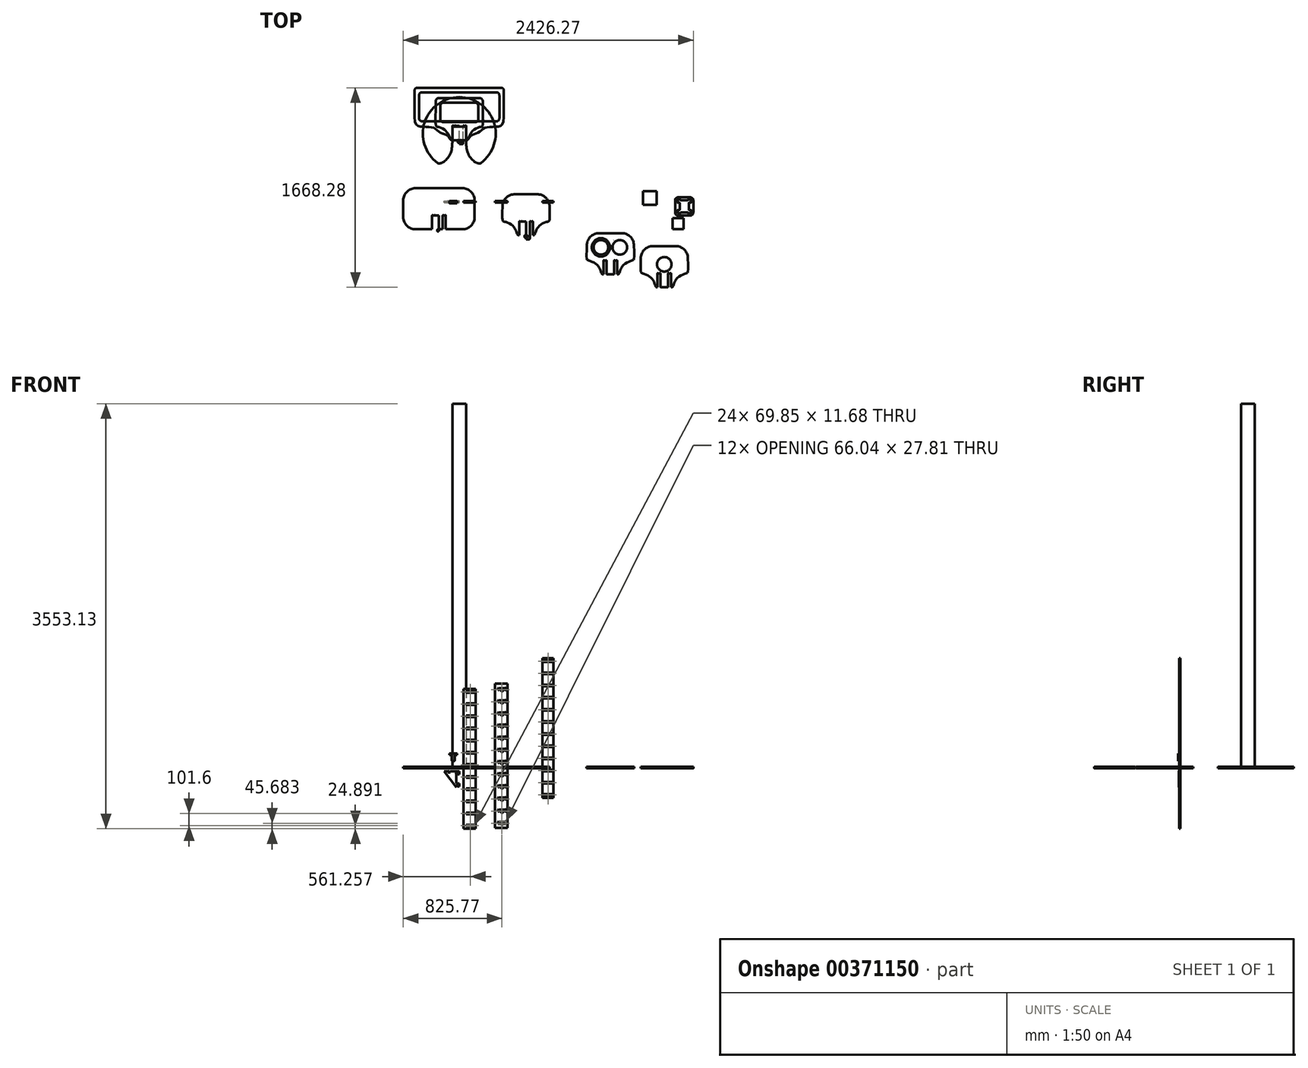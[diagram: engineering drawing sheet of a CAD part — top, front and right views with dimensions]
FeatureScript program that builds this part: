
annotation { "Feature Type Name" : "Feature", "Feature Type Description" : "" }
export const myFeature = defineFeature(function(context is Context, id is Id, definition is map)
    precondition{}
    {
        {
            var Q0;
            Q0=qCreatedBy(makeId("Top.planeOp"),FACE);
            var sketch = newSketch(context, id + "F0", { "sketchPlane" : qUnion([Q0])});
            skLineSegment(sketch, "E0.bottom", {"start": v(-334.1, 107.17) * mm, "end": v(59.6, 107.17) * mm});
            skLineSegment(sketch, "E0.top", {"start": v(-334.1, -235.73) * mm, "end": v(59.6, -235.73) * mm});
            skLineSegment(sketch, "E0.left", {"start": v(-435.7, 5.57) * mm, "end": v(-435.7, -134.13) * mm});
            skLineSegment(sketch, "E0.right", {"start": v(161.2, 5.57) * mm, "end": v(161.2, -134.13) * mm});
            skPoint(sketch, "E1.visualSharp", {"position": v(161.2, 107.17) * mm});
            skArc(sketch, "E1.filletArc", {"start": v(161.2, 5.57) * mm, "mid": v(131.45, 77.42) * mm, "end": v(59.6, 107.17) * mm});
            skPoint(sketch, "E2.visualSharp", {"position": v(-435.7, 107.17) * mm});
            skArc(sketch, "E2.filletArc", {"start": v(-334.1, 107.17) * mm, "mid": v(-405.93, 77.42) * mm, "end": v(-435.7, 5.57) * mm});
            skPoint(sketch, "E3.visualSharp", {"position": v(-435.7, -235.73) * mm});
            skArc(sketch, "E3.filletArc", {"start": v(-435.7, -134.13) * mm, "mid": v(-405.93, -205.97) * mm, "end": v(-334.1, -235.73) * mm});
            skPoint(sketch, "E4.visualSharp", {"position": v(161.2, -235.73) * mm});
            skArc(sketch, "E4.filletArc", {"start": v(59.6, -235.73) * mm, "mid": v(131.45, -205.97) * mm, "end": v(161.2, -134.13) * mm});
            skLineSegment(sketch, "E5", {"start": v(-137.24, -235.73) * mm, "end": v(-137.24, 107.17) * mm, "construction": true});
            skLineSegment(sketch, "E6", {"start": v(-137.24, -235.73) * mm, "end": v(-137.24, -305.02) * mm, "construction": true});
            skLineSegment(sketch, "E7.bottom", {"start": v(-137.24, -270.37) * mm, "end": v(-115.02, -270.37) * mm});
            skLineSegment(sketch, "E7.top", {"start": v(-137.24, -121.43) * mm, "end": v(-105.5, -121.43) * mm});
            skLineSegment(sketch, "E7.left", {"start": v(-137.24, -270.37) * mm, "end": v(-137.24, -121.43) * mm});
            skLineSegment(sketch, "E7.right", {"start": v(-105.5, -260.85) * mm, "end": v(-105.5, -121.43) * mm});
            skLineSegment(sketch, "E8.bottom", {"start": v(-105.5, -121.43) * mm, "end": v(-80.1, -121.43) * mm});
            skLineSegment(sketch, "E8.top", {"start": v(-105.5, -235.73) * mm, "end": v(-80.1, -235.73) * mm});
            skLineSegment(sketch, "E8.left", {"start": v(-105.5, -121.43) * mm, "end": v(-105.5, -235.73) * mm});
            skLineSegment(sketch, "E8.right", {"start": v(-80.1, -121.43) * mm, "end": v(-80.1, -235.73) * mm});
            skLineSegment(sketch, "E9.bottom", {"start": v(-137.24, -235.73) * mm, "end": v(-127.72, -235.73) * mm});
            skLineSegment(sketch, "E9.top", {"start": v(-137.24, -254.5) * mm, "end": v(-127.72, -254.5) * mm});
            skLineSegment(sketch, "E9.left", {"start": v(-137.24, -235.73) * mm, "end": v(-137.24, -254.5) * mm});
            skLineSegment(sketch, "E9.right", {"start": v(-124.54, -238.9) * mm, "end": v(-124.54, -251.32) * mm});
            skArc(sketch, "E10", {"start": v(-99.14, -121.43) * mm, "mid": v(-102.32, -118.25) * mm, "end": v(-105.5, -121.43) * mm});
            skArc(sketch, "E11", {"start": v(-80.1, -121.43) * mm, "mid": v(-83.27, -118.25) * mm, "end": v(-86.44, -121.43) * mm});
            skPoint(sketch, "E12.visualSharp", {"position": v(-124.54, -254.5) * mm});
            skArc(sketch, "E12.filletArc", {"start": v(-127.72, -254.5) * mm, "mid": v(-125.47, -253.57) * mm, "end": v(-124.54, -251.32) * mm});
            skPoint(sketch, "E13.visualSharp", {"position": v(-124.54, -235.73) * mm});
            skArc(sketch, "E13.filletArc", {"start": v(-124.54, -238.9) * mm, "mid": v(-125.47, -236.66) * mm, "end": v(-127.72, -235.73) * mm});
            skPoint(sketch, "E14.visualSharp", {"position": v(-105.5, -270.37) * mm});
            skArc(sketch, "E14.filletArc", {"start": v(-115.02, -270.37) * mm, "mid": v(-108.28, -267.58) * mm, "end": v(-105.5, -260.85) * mm});
            skArc(sketch, "E15.MirrorCS", {"start": v(-149.94, -238.9) * mm, "mid": v(-149.01, -236.66) * mm, "end": v(-146.77, -235.73) * mm});
            skLineSegment(sketch, "E16.MirrorCS", {"start": v(-137.24, -235.73) * mm, "end": v(-146.77, -235.73) * mm});
            skArc(sketch, "E17.MirrorCS", {"start": v(-146.77, -254.5) * mm, "mid": v(-149.01, -253.57) * mm, "end": v(-149.94, -251.32) * mm});
            skArc(sketch, "E18.MirrorCS", {"start": v(-175.34, -121.43) * mm, "mid": v(-172.17, -118.25) * mm, "end": v(-169, -121.43) * mm});
            skLineSegment(sketch, "E19.MirrorCS", {"start": v(-169, -121.43) * mm, "end": v(-194.4, -121.43) * mm});
            skLineSegment(sketch, "E20.MirrorCS", {"start": v(-137.24, -254.5) * mm, "end": v(-146.77, -254.5) * mm});
            skArc(sketch, "E21.MirrorCS", {"start": v(-194.4, -121.43) * mm, "mid": v(-191.22, -118.25) * mm, "end": v(-188.04, -121.43) * mm});
            skArc(sketch, "E22.MirrorCS", {"start": v(-159.47, -270.37) * mm, "mid": v(-166.2, -267.58) * mm, "end": v(-169, -260.85) * mm});
            skLineSegment(sketch, "E23.MirrorCS", {"start": v(-169, -121.43) * mm, "end": v(-169, -235.73) * mm});
            skLineSegment(sketch, "E24.MirrorCS", {"start": v(-169, -235.73) * mm, "end": v(-194.4, -235.73) * mm});
            skLineSegment(sketch, "E25.MirrorCS", {"start": v(-137.24, -270.37) * mm, "end": v(-159.47, -270.37) * mm});
            skLineSegment(sketch, "E26.MirrorCS", {"start": v(-149.94, -238.9) * mm, "end": v(-149.94, -251.32) * mm});
            skPoint(sketch, "E27.MirrorP", {"position": v(-149.94, -235.73) * mm});
            skLineSegment(sketch, "E28.MirrorCS", {"start": v(-137.24, -121.43) * mm, "end": v(-169, -121.43) * mm});
            skPoint(sketch, "E29.MirrorP", {"position": v(-169, -270.37) * mm});
            skLineSegment(sketch, "E30.MirrorCS", {"start": v(-169, -260.85) * mm, "end": v(-169, -121.43) * mm});
            skPoint(sketch, "E31.MirrorP", {"position": v(-149.94, -254.5) * mm});
            skLineSegment(sketch, "E32.MirrorCS", {"start": v(-194.4, -121.43) * mm, "end": v(-194.4, -235.73) * mm});
            skSolve(sketch);
        }
        {
            var Q0;
            {var subQ3=sQuery(id+"F0.wireOp",EDGE,"E15.MirrorCS");Q0=makeQuery(id+"F0.imprint","IMPRINT",FACE,{"disambiguationData":[TD([[makeQuery(id+"F0.imprint","IMPRINT",EDGE,{"derivedFrom":subQ3}),1.0]])]});}
            var Q1;
            {var subQ0=sQuery(id+"F0.wireOp",EDGE,"E7.right");Q1=makeQuery(id+"F0.imprint","IMPRINT",FACE,{"disambiguationData":[TD([[makeQuery(id+"F0.imprint","IMPRINT",EDGE,{"derivedFrom":subQ0}),1.0]])]});}
            var Q2;
            {var subQ2=sQuery(id+"F0.wireOp",EDGE,"E16.MirrorCS");Q2=makeQuery(id+"F0.imprint","IMPRINT",FACE,{"disambiguationData":[TD([[makeQuery(id+"F0.imprint","IMPRINT",EDGE,{"derivedFrom":subQ2}),-1.0]])]});}
            var Q3;
            {var subQ2=sQuery(id+"F0.wireOp",EDGE,"E7.top");Q3=makeQuery(id+"F0.imprint","IMPRINT",FACE,{"disambiguationData":[TD([[makeQuery(id+"F0.imprint","IMPRINT",EDGE,{"derivedFrom":subQ2}),-1.0]])]});}
            var Q4;
            Q4=makeQuery(id+"F0.imprint","IMPRINT",FACE,{"disambiguationData":[TD([[makeQuery(id+"F0.imprint","IMPRINT",EDGE,{"derivedFrom":sQuery(id+"F0.wireOp",EDGE,"E0.bottom")}),-1.0]])]});
            extrude(context, id + "F1", {"entities" : qUnion([Q0, Q1, Q2, Q3, Q4]), "depth" : 11.9 * mm});
        }
        {
            var Q0;
            Q0=qCreatedBy(makeId("Top.planeOp"),FACE);
            var sketch = newSketch(context, id + "F2", { "sketchPlane" : qUnion([Q0])});
            skPoint(sketch, "E33.visualSharp", {"position": v(788.15, 56.35) * mm});
            skArc(sketch, "E33.filletArc", {"start": v(788.15, -45.25) * mm, "mid": v(758.4, 26.59) * mm, "end": v(686.55, 56.35) * mm});
            skPoint(sketch, "E34.visualSharp", {"position": v(788.15, -286.55) * mm});
            skLineSegment(sketch, "E35", {"start": v(591.3, -286.55) * mm, "end": v(591.3, 56.35) * mm, "construction": true});
            skLineSegment(sketch, "E36", {"start": v(591.3, -286.55) * mm, "end": v(591.3, -369.1) * mm, "construction": true});
            skLineSegment(sketch, "E37.top", {"start": v(591.3, -172.25) * mm, "end": v(623.05, -172.25) * mm});
            skLineSegment(sketch, "E37.left", {"start": v(591.3, -327.83) * mm, "end": v(591.3, -172.25) * mm});
            skLineSegment(sketch, "E37.right", {"start": v(623.05, -311.97) * mm, "end": v(623.05, -172.25) * mm});
            skLineSegment(sketch, "E38.bottom", {"start": v(623.05, -172.25) * mm, "end": v(648.45, -172.25) * mm});
            skLineSegment(sketch, "E38.top", {"start": v(623.05, -286.55) * mm, "end": v(648.45, -286.55) * mm});
            skLineSegment(sketch, "E38.left", {"start": v(623.05, -172.25) * mm, "end": v(623.05, -286.55) * mm});
            skLineSegment(sketch, "E38.right", {"start": v(648.45, -172.25) * mm, "end": v(648.45, -286.55) * mm});
            skLineSegment(sketch, "E39.bottom", {"start": v(591.3, -286.55) * mm, "end": v(600.7, -286.55) * mm});
            skLineSegment(sketch, "E39.left", {"start": v(591.3, -286.55) * mm, "end": v(591.3, -311.95) * mm});
            skArc(sketch, "E40", {"start": v(629.4, -172.25) * mm, "mid": v(626.23, -169.08) * mm, "end": v(623.05, -172.25) * mm});
            skPoint(sketch, "E41.visualSharp", {"position": v(604, -311.95) * mm});
            skLineSegment(sketch, "E41.filletArc", {"start": v(604, -311.95) * mm, "end": v(604, -311.95) * mm});
            skPoint(sketch, "E42.visualSharp", {"position": v(604, -286.55) * mm});
            skArc(sketch, "E42.filletArc", {"start": v(604, -289.87) * mm, "mid": v(603.03, -287.52) * mm, "end": v(600.7, -286.55) * mm});
            skPoint(sketch, "E43.visualSharp", {"position": v(623.05, -327.83) * mm});
            skArc(sketch, "E43.filletArc", {"start": v(613.53, -321.48) * mm, "mid": v(620.26, -318.69) * mm, "end": v(623.05, -311.95) * mm});
            skArc(sketch, "E44.MirrorCS", {"start": v(578.6, -289.87) * mm, "mid": v(579.57, -287.52) * mm, "end": v(581.92, -286.55) * mm});
            skLineSegment(sketch, "E45.MirrorCS", {"start": v(591.3, -286.55) * mm, "end": v(581.92, -286.55) * mm});
            skLineSegment(sketch, "E46.MirrorCS", {"start": v(578.6, -311.95) * mm, "end": v(578.6, -311.95) * mm});
            skArc(sketch, "E47.MirrorCS", {"start": v(553.2, -172.25) * mm, "mid": v(556.38, -169.08) * mm, "end": v(559.55, -172.25) * mm});
            skLineSegment(sketch, "E48.MirrorCS", {"start": v(559.55, -172.25) * mm, "end": v(534.15, -172.25) * mm});
            skArc(sketch, "E49.MirrorCS", {"start": v(569.08, -321.48) * mm, "mid": v(562.34, -318.69) * mm, "end": v(559.55, -311.95) * mm});
            skLineSegment(sketch, "E50.MirrorCS", {"start": v(559.55, -172.25) * mm, "end": v(559.55, -286.55) * mm});
            skLineSegment(sketch, "E51.MirrorCS", {"start": v(559.55, -286.55) * mm, "end": v(534.15, -286.55) * mm});
            skPoint(sketch, "E52.MirrorP", {"position": v(578.6, -286.55) * mm});
            skLineSegment(sketch, "E53.MirrorCS", {"start": v(591.3, -172.25) * mm, "end": v(559.55, -172.25) * mm});
            skLineSegment(sketch, "E54.MirrorCS", {"start": v(559.55, -311.95) * mm, "end": v(559.55, -172.25) * mm});
            skLineSegment(sketch, "E55.MirrorCS", {"start": v(534.15, -172.25) * mm, "end": v(534.15, -286.55) * mm});
            skLineSegment(sketch, "E56.MirrorCS", {"start": v(591.3, -321.48) * mm, "end": v(613.53, -321.48) * mm});
            skLineSegment(sketch, "E57.MirrorCS", {"start": v(591.3, -321.48) * mm, "end": v(569.08, -321.48) * mm});
            skFitSpline(sketch, "E58", {"points": [v(648.45, -286.55) * mm, v(655.33, -286.55) * mm, v(665.07, -276.72) * mm, v(673.52, -253) * mm, v(688.14, -225.4) * mm, v(716.4, -196.15) * mm, v(761.89, -175.36) * mm, v(775.2, -171.46) * mm, v(786.25, -163.02) * mm, v(790.22, -124.89) * mm, v(788.15, -45.25) * mm], "startDerivative": vector(133.06, -25.03) * mm, "endDerivative": vector(-44.6, 1613.14) * mm});
            skFitSpline(sketch, "E59.MirrorCS", {"points": [v(534.15, -286.55) * mm, v(527.28, -286.55) * mm, v(517.53, -276.72) * mm, v(509.09, -253) * mm, v(494.47, -225.4) * mm, v(466.2, -196.15) * mm, v(420.72, -175.36) * mm, v(407.4, -171.46) * mm, v(396.36, -163.02) * mm, v(392.39, -124.89) * mm, v(394.45, -45.25) * mm], "startDerivative": vector(-133.06, -25.03) * mm, "endDerivative": vector(44.6, 1613.14) * mm});
            skLineSegment(sketch, "E60.MirrorCS", {"start": v(686.55, 56.35) * mm, "end": v(496.05, 56.35) * mm});
            skPoint(sketch, "E61.MirrorP", {"position": v(394.45, 56.35) * mm});
            skArc(sketch, "E62.MirrorCS", {"start": v(394.45, -45.25) * mm, "mid": v(424.21, 26.59) * mm, "end": v(496.05, 56.35) * mm});
            skPoint(sketch, "E63.MirrorP", {"position": v(394.45, -286.55) * mm});
            skArc(sketch, "E64", {"start": v(648.45, -172.25) * mm, "mid": v(645.28, -169.08) * mm, "end": v(642.1, -172.25) * mm});
            skArc(sketch, "E65", {"start": v(540.5, -172.25) * mm, "mid": v(537.33, -169.08) * mm, "end": v(534.15, -172.25) * mm});
            skLineSegment(sketch, "E66", {"start": v(578.6, -289.87) * mm, "end": v(578.6, -302.15) * mm});
            skLineSegment(sketch, "E67", {"start": v(581.78, -305.32) * mm, "end": v(600.83, -305.32) * mm});
            skLineSegment(sketch, "E68", {"start": v(604, -302.15) * mm, "end": v(604, -289.87) * mm});
            skPoint(sketch, "E69.visualSharp", {"position": v(578.6, -305.32) * mm});
            skArc(sketch, "E69.filletArc", {"start": v(578.6, -302.15) * mm, "mid": v(579.53, -304.4) * mm, "end": v(581.78, -305.32) * mm});
            skPoint(sketch, "E70.visualSharp", {"position": v(604, -305.32) * mm});
            skArc(sketch, "E70.filletArc", {"start": v(600.83, -305.32) * mm, "mid": v(603.07, -304.4) * mm, "end": v(604, -302.15) * mm});
            skLineSegment(sketch, "E71", {"start": v(623.05, -311.97) * mm, "end": v(623.05, -286.55) * mm});
            skPoint(sketch, "E72.orphan", {"position": v(559.55, -318.3) * mm});
            skPoint(sketch, "E73.orphan", {"position": v(623.05, -318.3) * mm});
            skSolve(sketch);
        }
        {
            var Q0;
            {var subQ1=sQuery(id+"F2.wireOp",EDGE,"E37.top");Q0=makeQuery(id+"F2.imprint","IMPRINT",FACE,{"disambiguationData":[TD([[makeQuery(id+"F2.imprint","IMPRINT",EDGE,{"derivedFrom":subQ1}),-1.0]])]});}
            var Q1;
            Q1=makeQuery(id+"F2.imprint","IMPRINT",FACE,{"disambiguationData":[TD([[makeQuery(id+"F2.imprint","IMPRINT",EDGE,{"derivedFrom":sQuery(id+"F2.wireOp",EDGE,"E44.MirrorCS")}),1.0]])]});
            var Q2;
            Q2=makeQuery(id+"F2.imprint","IMPRINT",FACE,{"disambiguationData":[TD([[makeQuery(id+"F2.imprint","IMPRINT",EDGE,{"derivedFrom":sQuery(id+"F2.wireOp",EDGE,"E33.filletArc")}),1.0]])]});
            extrude(context, id + "F3", {"entities" : qUnion([Q0, Q1, Q2]), "depth" : 11.9 * mm});
        }
        {
            var Q0;
            Q0=qCreatedBy(makeId("Top.planeOp"),FACE);
            var sketch = newSketch(context, id + "F4", { "sketchPlane" : qUnion([Q0])});
            skLineSegment(sketch, "E74.bottom", {"start": v(-24.65, 621.06) * mm, "end": v(89.65, 621.06) * mm});
            skLineSegment(sketch, "E74.top", {"start": v(-24.65, 506.76) * mm, "end": v(89.65, 506.76) * mm});
            skLineSegment(sketch, "E74.left", {"start": v(-24.65, 621.06) * mm, "end": v(-24.65, 506.76) * mm});
            skLineSegment(sketch, "E74.right", {"start": v(89.65, 621.06) * mm, "end": v(89.65, 506.76) * mm});
            skSolve(sketch);
        }
        {
            var Q0;
            Q0 = qSketchRegion(id + "F4", true);
            extrude(context, id + "F5", {"entities" : qUnion([Q0]), "depth" : 3048 * mm});
        }
        {
            var Q0;
            Q0=qCreatedBy(makeId("Front.planeOp"),FACE);
            var sketch = newSketch(context, id + "F6", { "sketchPlane" : qUnion([Q0])});
            skLineSegment(sketch, "E75", {"start": v(-93.52, -26.57) * mm, "end": v(8.08, -26.57) * mm});
            skLineSegment(sketch, "E76", {"start": v(8.08, -26.57) * mm, "end": v(8.08, -159.92) * mm});
            skLineSegment(sketch, "E77", {"start": v(8.08, -159.92) * mm, "end": v(-93.52, -26.57) * mm});
            skLineSegment(sketch, "E78", {"start": v(8.08, -26.57) * mm, "end": v(33.48, -26.57) * mm});
            skLineSegment(sketch, "E79", {"start": v(33.48, -26.57) * mm, "end": v(33.48, -51.97) * mm});
            skLineSegment(sketch, "E80", {"start": v(33.48, -51.97) * mm, "end": v(19.64, -51.97) * mm});
            skLineSegment(sketch, "E81", {"start": v(19.64, -51.97) * mm, "end": v(19.64, -39.27) * mm});
            skLineSegment(sketch, "E82", {"start": v(19.64, -39.27) * mm, "end": v(8.08, -39.27) * mm});
            skLineSegment(sketch, "E83", {"start": v(8.08, -128.17) * mm, "end": v(33.48, -128.17) * mm});
            skLineSegment(sketch, "E84", {"start": v(33.48, -128.17) * mm, "end": v(33.48, -153.57) * mm});
            skLineSegment(sketch, "E85", {"start": v(33.48, -153.57) * mm, "end": v(19.64, -153.57) * mm});
            skLineSegment(sketch, "E86", {"start": v(19.64, -153.57) * mm, "end": v(19.64, -140.87) * mm});
            skLineSegment(sketch, "E87", {"start": v(19.64, -140.87) * mm, "end": v(8.08, -140.87) * mm});
            skLineSegment(sketch, "E88", {"start": v(-62.12, -26.57) * mm, "end": v(-49.42, -23.4) * mm});
            skLineSegment(sketch, "E89", {"start": v(-49.42, -23.4) * mm, "end": v(-49.42, -26.57) * mm});
            skLineSegment(sketch, "E90", {"start": v(-49.42, -26.57) * mm, "end": v(-49.42, -26.57) * mm});
            skLineSegment(sketch, "E91", {"start": v(-52.6, -29.75) * mm, "end": v(-59.07, -29.75) * mm});
            skLineSegment(sketch, "E92", {"start": v(-62.25, -32.92) * mm, "end": v(-62.25, -32.92) * mm});
            skLineSegment(sketch, "E93", {"start": v(-59.07, -36.1) * mm, "end": v(-46.25, -36.1) * mm});
            skLineSegment(sketch, "E94", {"start": v(-43.07, -32.92) * mm, "end": v(-43.07, -26.57) * mm});
            skPoint(sketch, "E95.visualSharp", {"position": v(-43.07, -36.1) * mm});
            skArc(sketch, "E95.filletArc", {"start": v(-46.25, -36.1) * mm, "mid": v(-44, -35.17) * mm, "end": v(-43.07, -32.92) * mm});
            skPoint(sketch, "E96.visualSharp", {"position": v(-49.42, -29.75) * mm});
            skArc(sketch, "E96.filletArc", {"start": v(-52.6, -29.75) * mm, "mid": v(-50.35, -28.82) * mm, "end": v(-49.42, -26.57) * mm});
            skPoint(sketch, "E97.visualSharp", {"position": v(-62.25, -29.75) * mm});
            skArc(sketch, "E97.filletArc", {"start": v(-59.07, -29.75) * mm, "mid": v(-61.32, -30.68) * mm, "end": v(-62.25, -32.92) * mm});
            skPoint(sketch, "E98.visualSharp", {"position": v(-62.25, -36.1) * mm});
            skArc(sketch, "E98.filletArc", {"start": v(-62.25, -32.92) * mm, "mid": v(-61.32, -35.17) * mm, "end": v(-59.07, -36.1) * mm});
            skArc(sketch, "E99", {"start": v(8.08, -39.27) * mm, "mid": v(4.9, -42.45) * mm, "end": v(8.08, -45.62) * mm});
            skArc(sketch, "E100", {"start": v(19.64, -45.62) * mm, "mid": v(22.82, -42.45) * mm, "end": v(19.64, -39.27) * mm});
            skArc(sketch, "E101", {"start": v(8.08, -140.87) * mm, "mid": v(4.9, -144.05) * mm, "end": v(8.08, -147.22) * mm});
            skArc(sketch, "E102", {"start": v(19.64, -147.22) * mm, "mid": v(22.82, -144.05) * mm, "end": v(19.64, -140.87) * mm});
            skSolve(sketch);
        }
        {
            var Q0;
            {var subQ0=sQuery(id+"F6.wireOp",EDGE,"E88");Q0=makeQuery(id+"F6.imprint","IMPRINT",FACE,{"disambiguationData":[TD([[makeQuery(id+"F6.imprint","IMPRINT",EDGE,{"derivedFrom":subQ0}),-1.0]])]});}
            var Q1;
            {var subQ1=sQuery(id+"F6.wireOp",EDGE,"E78");Q1=makeQuery(id+"F6.imprint","IMPRINT",FACE,{"disambiguationData":[TD([[makeQuery(id+"F6.imprint","IMPRINT",EDGE,{"derivedFrom":subQ1}),-1.0]])]});}
            var Q2;
            {var subQ1=sQuery(id+"F6.wireOp",EDGE,"E83");Q2=makeQuery(id+"F6.imprint","IMPRINT",FACE,{"disambiguationData":[TD([[makeQuery(id+"F6.imprint","IMPRINT",EDGE,{"derivedFrom":subQ1}),-1.0]])]});}
            var Q3;
            {var subQ0=sQuery(id+"F6.wireOp",EDGE,"E77");Q3=makeQuery(id+"F6.imprint","IMPRINT",FACE,{"disambiguationData":[TD([[makeQuery(id+"F6.imprint","IMPRINT",EDGE,{"derivedFrom":subQ0}),-1.0]])]});}
            extrude(context, id + "F7", {"entities" : qUnion([Q0, Q1, Q2, Q3]), "depth" : 11.9 * mm});
        }
        {
            var Q0;
            Q0=qCreatedBy(makeId("Top.planeOp"),FACE);
            var sketch = newSketch(context, id + "F8", { "sketchPlane" : qUnion([Q0])});
            skLineSegment(sketch, "E103", {"start": v(32.55, 506.79) * mm, "end": v(32.55, 849.69) * mm, "construction": true});
            skLineSegment(sketch, "E104", {"start": v(32.55, 506.79) * mm, "end": v(32.55, 424.24) * mm, "construction": true});
            skLineSegment(sketch, "E105.bottom", {"start": v(32.55, 475.04) * mm, "end": v(54.77, 475.04) * mm});
            skLineSegment(sketch, "E105.top", {"start": v(32.55, 621.09) * mm, "end": v(64.3, 621.09) * mm});
            skLineSegment(sketch, "E105.left", {"start": v(32.55, 465.51) * mm, "end": v(32.55, 621.09) * mm});
            skLineSegment(sketch, "E105.right", {"start": v(64.3, 506.79) * mm, "end": v(64.3, 621.09) * mm});
            skLineSegment(sketch, "E106.bottom", {"start": v(64.3, 621.09) * mm, "end": v(89.7, 621.09) * mm});
            skLineSegment(sketch, "E106.top", {"start": v(64.3, 506.79) * mm, "end": v(89.7, 506.79) * mm});
            skLineSegment(sketch, "E106.left", {"start": v(64.3, 621.09) * mm, "end": v(64.3, 506.79) * mm});
            skLineSegment(sketch, "E106.right", {"start": v(89.7, 621.09) * mm, "end": v(89.7, 506.79) * mm});
            skLineSegment(sketch, "E107.bottom", {"start": v(32.55, 506.79) * mm, "end": v(41.94, 506.79) * mm});
            skLineSegment(sketch, "E107.left", {"start": v(32.55, 506.79) * mm, "end": v(32.55, 481.39) * mm});
            skArc(sketch, "E108", {"start": v(70.65, 621.09) * mm, "mid": v(67.47, 624.26) * mm, "end": v(64.3, 621.09) * mm});
            skPoint(sketch, "E109.visualSharp", {"position": v(45.25, 481.39) * mm});
            skPoint(sketch, "E110.visualSharp", {"position": v(45.25, 506.79) * mm});
            skArc(sketch, "E110.filletArc", {"start": v(45.25, 503.47) * mm, "mid": v(44.28, 505.82) * mm, "end": v(41.94, 506.79) * mm});
            skPoint(sketch, "E111.visualSharp", {"position": v(64.3, 465.51) * mm});
            skArc(sketch, "E111.filletArc", {"start": v(54.77, 475.04) * mm, "mid": v(61.5, 477.83) * mm, "end": v(64.3, 484.56) * mm});
            skLineSegment(sketch, "E112.MirrorCS", {"start": v(78.45, 423.4) * mm, "end": v(78.45, 423.4) * mm});
            skArc(sketch, "E113", {"start": v(89.7, 621.09) * mm, "mid": v(86.52, 624.26) * mm, "end": v(83.35, 621.09) * mm});
            skLineSegment(sketch, "E114", {"start": v(45.25, 491.18) * mm, "end": v(45.25, 503.47) * mm});
            skPoint(sketch, "E115.visualSharp", {"position": v(45.25, 478.07) * mm});
            skArc(sketch, "E115.filletArc", {"start": v(42.07, 488) * mm, "mid": v(44.32, 488.94) * mm, "end": v(45.25, 491.18) * mm});
            skLineSegment(sketch, "E116", {"start": v(64.3, 484.56) * mm, "end": v(64.3, 506.79) * mm});
            skCircle(sketch, "E117", {"center": v(32.55, 563.94) * mm, "radius": 304.8 * mm});
            skPoint(sketch, "E117.centerSnap0", {"position": v(64.3, 563.94) * mm});
            skFitSpline(sketch, "E118", {"points": [v(89.7, 506.79) * mm, v(109.77, 389.43) * mm, v(176.95, 319.57) * mm, v(213.65, 318.78) * mm], "startDerivative": vector(9.59, -299.6) * mm, "endDerivative": vector(116.84, 83.15) * mm});
            skLineSegment(sketch, "E119.MirrorCS", {"start": v(32.55, 506.79) * mm, "end": v(23.16, 506.79) * mm});
            skArc(sketch, "E120.MirrorCS", {"start": v(19.85, 503.47) * mm, "mid": v(20.82, 505.82) * mm, "end": v(23.16, 506.79) * mm});
            skArc(sketch, "E121.MirrorCS", {"start": v(23.02, 488) * mm, "mid": v(20.78, 488.94) * mm, "end": v(19.85, 491.18) * mm});
            skArc(sketch, "E122.MirrorCS", {"start": v(-24.6, 621.09) * mm, "mid": v(-21.43, 624.26) * mm, "end": v(-18.25, 621.09) * mm});
            skArc(sketch, "E123.MirrorCS", {"start": v(-5.55, 621.09) * mm, "mid": v(-2.38, 624.26) * mm, "end": v(0.8, 621.09) * mm});
            skArc(sketch, "E124.MirrorCS", {"start": v(10.32, 475.04) * mm, "mid": v(3.59, 477.83) * mm, "end": v(0.8, 484.56) * mm});
            skLineSegment(sketch, "E125.MirrorCS", {"start": v(0.8, 621.09) * mm, "end": v(-24.6, 621.09) * mm});
            skPoint(sketch, "E126.MirrorP", {"position": v(0.8, 465.51) * mm});
            skPoint(sketch, "E127.MirrorP", {"position": v(19.85, 506.79) * mm});
            skLineSegment(sketch, "E128.MirrorCS", {"start": v(0.8, 484.56) * mm, "end": v(0.8, 506.79) * mm});
            skPoint(sketch, "E129.MirrorP", {"position": v(19.85, 481.39) * mm});
            skLineSegment(sketch, "E130.MirrorCS", {"start": v(0.8, 484.56) * mm, "end": v(0.8, 621.09) * mm});
            skLineSegment(sketch, "E131.MirrorCS", {"start": v(32.55, 475.04) * mm, "end": v(10.32, 475.04) * mm});
            skLineSegment(sketch, "E132.MirrorCS", {"start": v(32.55, 621.09) * mm, "end": v(0.8, 621.09) * mm});
            skPoint(sketch, "E133.MirrorP", {"position": v(19.85, 478.07) * mm});
            skPoint(sketch, "E134.MirrorP", {"position": v(0.8, 563.94) * mm});
            skLineSegment(sketch, "E135.MirrorCS", {"start": v(0.8, 506.79) * mm, "end": v(-24.6, 506.79) * mm});
            skLineSegment(sketch, "E136.MirrorCS", {"start": v(0.8, 621.09) * mm, "end": v(0.8, 506.79) * mm});
            skFitSpline(sketch, "E137.MirrorCS", {"points": [v(-24.6, 506.79) * mm, v(-44.68, 389.43) * mm, v(-111.86, 319.57) * mm, v(-148.56, 318.78) * mm], "startDerivative": vector(-9.59, -299.6) * mm, "endDerivative": vector(-116.84, 83.15) * mm});
            skLineSegment(sketch, "E138.MirrorCS", {"start": v(19.85, 491.18) * mm, "end": v(19.85, 503.47) * mm});
            skLineSegment(sketch, "E139.MirrorCS", {"start": v(-24.6, 621.09) * mm, "end": v(-24.6, 506.79) * mm});
            skLineSegment(sketch, "E140", {"start": v(23.02, 488) * mm, "end": v(42.07, 488) * mm});
            skPoint(sketch, "E141.orphan", {"position": v(0.8, 475.04) * mm});
            skPoint(sketch, "E142.orphan", {"position": v(64.3, 475.04) * mm});
            skSolve(sketch);
        }
        {
            var Q0;
            Q0=makeQuery(id+"F8.imprint","IMPRINT",FACE,{"disambiguationData":[TD([[makeQuery(id+"F8.imprint","IMPRINT",EDGE,{"derivedFrom":sQuery(id+"F8.wireOp",EDGE,"E105.top")}),1.0]])]});
            var Q1;
            {var subQ5=sQuery(id+"F8.wireOp",EDGE,"E105.top");Q1=makeQuery(id+"F8.imprint","IMPRINT",FACE,{"disambiguationData":[TD([[makeQuery(id+"F8.imprint","IMPRINT",EDGE,{"derivedFrom":subQ5}),-1.0]])]});}
            var Q2;
            Q2=makeQuery(id+"F8.imprint","IMPRINT",FACE,{"disambiguationData":[TD([[makeQuery(id+"F8.imprint","IMPRINT",EDGE,{"derivedFrom":sQuery(id+"F8.wireOp",EDGE,"E120.MirrorCS")}),1.0]])]});
            extrude(context, id + "F9", {"entities" : qUnion([Q0, Q1, Q2]), "depth" : 11.9 * mm});
        }
        {
            var Q0;
            Q0=qCreatedBy(makeId("Top.planeOp"),FACE);
            var sketch = newSketch(context, id + "F10", { "sketchPlane" : qUnion([Q0])});
            skPoint(sketch, "E143.visualSharp", {"position": v(229.42, 860.4) * mm});
            skPoint(sketch, "E144.visualSharp", {"position": v(229.42, 506.9) * mm});
            skLineSegment(sketch, "E145", {"start": v(32.57, 506.9) * mm, "end": v(32.57, 860.4) * mm, "construction": true});
            skLineSegment(sketch, "E146", {"start": v(32.57, 506.9) * mm, "end": v(32.57, 475.16) * mm, "construction": true});
            skLineSegment(sketch, "E147.top", {"start": v(32.57, 621.2) * mm, "end": v(64.32, 621.2) * mm});
            skLineSegment(sketch, "E147.left", {"start": v(32.57, 465.63) * mm, "end": v(32.57, 621.2) * mm});
            skLineSegment(sketch, "E147.right", {"start": v(64.32, 484.68) * mm, "end": v(64.32, 621.2) * mm});
            skLineSegment(sketch, "E148.bottom", {"start": v(64.32, 621.2) * mm, "end": v(89.72, 621.2) * mm});
            skLineSegment(sketch, "E148.top", {"start": v(64.32, 506.9) * mm, "end": v(89.72, 506.9) * mm});
            skLineSegment(sketch, "E148.left", {"start": v(64.32, 621.2) * mm, "end": v(64.32, 506.9) * mm});
            skLineSegment(sketch, "E148.right", {"start": v(89.72, 621.2) * mm, "end": v(89.72, 506.9) * mm});
            skLineSegment(sketch, "E149.bottom", {"start": v(32.57, 506.9) * mm, "end": v(41.95, 506.9) * mm});
            skLineSegment(sketch, "E149.left", {"start": v(32.57, 506.9) * mm, "end": v(32.57, 481.5) * mm});
            skArc(sketch, "E150", {"start": v(70.67, 621.2) * mm, "mid": v(67.5, 624.38) * mm, "end": v(64.32, 621.2) * mm});
            skPoint(sketch, "E151.visualSharp", {"position": v(45.27, 481.5) * mm});
            skLineSegment(sketch, "E151.filletArc", {"start": v(17.07, -63.32) * mm, "end": v(17.07, -63.32) * mm});
            skPoint(sketch, "E152.visualSharp", {"position": v(45.27, 506.9) * mm});
            skArc(sketch, "E152.filletArc", {"start": v(45.27, 503.6) * mm, "mid": v(44.3, 505.94) * mm, "end": v(41.95, 506.9) * mm});
            skPoint(sketch, "E153.visualSharp", {"position": v(64.32, 465.63) * mm});
            skArc(sketch, "E153.filletArc", {"start": v(54.8, 475.16) * mm, "mid": v(61.53, 477.95) * mm, "end": v(64.32, 484.68) * mm});
            skArc(sketch, "E154.MirrorCS", {"start": v(19.87, 503.6) * mm, "mid": v(20.84, 505.94) * mm, "end": v(23.18, 506.9) * mm});
            skLineSegment(sketch, "E155.MirrorCS", {"start": v(32.57, 506.9) * mm, "end": v(23.18, 506.9) * mm});
            skLineSegment(sketch, "E156.MirrorCS", {"start": v(-8.33, -63.32) * mm, "end": v(-8.33, -63.32) * mm});
            skArc(sketch, "E157.MirrorCS", {"start": v(-5.53, 621.2) * mm, "mid": v(-2.36, 624.38) * mm, "end": v(0.82, 621.2) * mm});
            skLineSegment(sketch, "E158.MirrorCS", {"start": v(0.82, 621.2) * mm, "end": v(-24.58, 621.2) * mm});
            skLineSegment(sketch, "E159.MirrorCS", {"start": v(0.82, 621.2) * mm, "end": v(0.82, 506.9) * mm});
            skLineSegment(sketch, "E160.MirrorCS", {"start": v(0.82, 506.9) * mm, "end": v(-24.58, 506.9) * mm});
            skLineSegment(sketch, "E161.MirrorCS", {"start": v(32.57, 475.16) * mm, "end": v(10.34, 475.16) * mm});
            skPoint(sketch, "E162.MirrorP", {"position": v(19.87, 506.9) * mm});
            skLineSegment(sketch, "E163.MirrorCS", {"start": v(32.57, 621.2) * mm, "end": v(0.82, 621.2) * mm});
            skPoint(sketch, "E164.MirrorP", {"position": v(0.82, 465.63) * mm});
            skLineSegment(sketch, "E165.MirrorCS", {"start": v(0.82, 484.68) * mm, "end": v(0.82, 621.2) * mm});
            skPoint(sketch, "E166.MirrorP", {"position": v(19.87, 481.5) * mm});
            skLineSegment(sketch, "E167.MirrorCS", {"start": v(-24.58, 621.2) * mm, "end": v(-24.58, 506.9) * mm});
            skArc(sketch, "E168.MirrorCS", {"start": v(10.34, 475.16) * mm, "mid": v(3.6, 477.95) * mm, "end": v(0.82, 484.68) * mm});
            skLineSegment(sketch, "E169.MirrorCS", {"start": v(32.57, 475.16) * mm, "end": v(54.8, 475.16) * mm});
            skFitSpline(sketch, "E170", {"points": [v(89.72, 506.9) * mm, v(96.6, 506.9) * mm, v(106.34, 516.74) * mm, v(114.78, 540.46) * mm, v(129.4, 568.07) * mm, v(157.67, 597.3) * mm, v(203.15, 618.1) * mm, v(216.47, 622) * mm, v(227.51, 630.45) * mm, v(231.48, 668.58) * mm, v(229.42, 758.8) * mm], "startDerivative": vector(133.06, -25.03) * mm, "endDerivative": vector(-44.6, 1613.14) * mm});
            skLineSegment(sketch, "E171.MirrorCS", {"start": v(127.82, 860.4) * mm, "end": v(-62.68, 860.4) * mm});
            skPoint(sketch, "E172.MirrorP", {"position": v(-164.28, 860.4) * mm});
            skPoint(sketch, "E173.MirrorP", {"position": v(-164.28, 506.9) * mm});
            skArc(sketch, "E174", {"start": v(89.72, 621.2) * mm, "mid": v(86.54, 624.38) * mm, "end": v(83.37, 621.2) * mm});
            skArc(sketch, "E175", {"start": v(-18.23, 621.2) * mm, "mid": v(-21.4, 624.38) * mm, "end": v(-24.58, 621.2) * mm});
            skLineSegment(sketch, "E176", {"start": v(19.87, 503.6) * mm, "end": v(19.87, 491.3) * mm});
            skLineSegment(sketch, "E177", {"start": v(23.04, 488.13) * mm, "end": v(42.1, 488.13) * mm});
            skLineSegment(sketch, "E178", {"start": v(45.27, 491.3) * mm, "end": v(45.27, 503.6) * mm});
            skPoint(sketch, "E179.visualSharp", {"position": v(19.87, 488.13) * mm});
            skArc(sketch, "E179.filletArc", {"start": v(19.87, 491.3) * mm, "mid": v(20.8, 489.06) * mm, "end": v(23.04, 488.13) * mm});
            skPoint(sketch, "E180.visualSharp", {"position": v(45.27, 488.13) * mm});
            skArc(sketch, "E180.filletArc", {"start": v(42.1, 488.13) * mm, "mid": v(44.34, 489.06) * mm, "end": v(45.27, 491.3) * mm});
            skLineSegment(sketch, "E181", {"start": v(64.32, 484.68) * mm, "end": v(64.32, 506.9) * mm});
            skLineSegment(sketch, "E182", {"start": v(229.42, 758.8) * mm, "end": v(229.42, 835) * mm});
            skLineSegment(sketch, "E183", {"start": v(127.82, 860.4) * mm, "end": v(204.02, 860.4) * mm});
            skArc(sketch, "E184.filletArc", {"start": v(229.42, 835) * mm, "mid": v(221.98, 852.95) * mm, "end": v(204.02, 860.4) * mm});
            skLineSegment(sketch, "E185.bottom", {"start": v(32.57, 822.3) * mm, "end": v(165.92, 822.3) * mm});
            skLineSegment(sketch, "E185.top", {"start": v(32.57, 659.3) * mm, "end": v(165.92, 659.3) * mm});
            skLineSegment(sketch, "E185.left", {"start": v(32.57, 822.3) * mm, "end": v(32.57, 659.3) * mm});
            skLineSegment(sketch, "E185.right", {"start": v(191.32, 796.9) * mm, "end": v(191.32, 684.7) * mm});
            skPoint(sketch, "E186.visualSharp", {"position": v(191.32, 659.3) * mm});
            skArc(sketch, "E186.filletArc", {"start": v(165.92, 659.3) * mm, "mid": v(183.88, 666.75) * mm, "end": v(191.32, 684.7) * mm});
            skPoint(sketch, "E187.visualSharp", {"position": v(191.32, 822.3) * mm});
            skArc(sketch, "E187.filletArc", {"start": v(191.32, 796.9) * mm, "mid": v(183.88, 814.85) * mm, "end": v(165.92, 822.3) * mm});
            skLineSegment(sketch, "E188.MirrorCS", {"start": v(-164.28, 758.8) * mm, "end": v(-164.28, 835) * mm});
            skArc(sketch, "E189.MirrorCS", {"start": v(-126.18, 796.9) * mm, "mid": v(-118.74, 814.85) * mm, "end": v(-100.78, 822.3) * mm});
            skPoint(sketch, "E190.MirrorP", {"position": v(-126.18, 659.3) * mm});
            skArc(sketch, "E191.MirrorCS", {"start": v(-100.78, 659.3) * mm, "mid": v(-118.74, 666.75) * mm, "end": v(-126.18, 684.7) * mm});
            skPoint(sketch, "E192.MirrorP", {"position": v(-126.18, 822.3) * mm});
            skLineSegment(sketch, "E193.MirrorCS", {"start": v(-62.68, 860.4) * mm, "end": v(127.82, 860.4) * mm});
            skLineSegment(sketch, "E194.MirrorCS", {"start": v(-126.18, 796.9) * mm, "end": v(-126.18, 684.7) * mm});
            skFitSpline(sketch, "E195.MirrorCS", {"points": [v(-24.58, 506.9) * mm, v(-31.46, 506.9) * mm, v(-41.2, 516.74) * mm, v(-49.65, 540.46) * mm, v(-64.27, 568.07) * mm, v(-92.53, 597.3) * mm, v(-138.02, 618.1) * mm, v(-151.34, 622) * mm, v(-162.38, 630.45) * mm, v(-166.35, 668.58) * mm, v(-164.28, 758.8) * mm], "startDerivative": vector(-133.06, -25.03) * mm, "endDerivative": vector(44.6, 1613.14) * mm});
            skLineSegment(sketch, "E196.MirrorCS", {"start": v(32.57, 659.3) * mm, "end": v(-100.78, 659.3) * mm});
            skArc(sketch, "E197.MirrorCS", {"start": v(-164.28, 835) * mm, "mid": v(-156.84, 852.95) * mm, "end": v(-138.88, 860.4) * mm});
            skLineSegment(sketch, "E198.MirrorCS", {"start": v(-62.68, 860.4) * mm, "end": v(-138.88, 860.4) * mm});
            skLineSegment(sketch, "E199.MirrorCS", {"start": v(32.57, 822.3) * mm, "end": v(-100.78, 822.3) * mm});
            skPoint(sketch, "E200.MirrorCS.end.orphan", {"position": v(10.34, 465.63) * mm});
            skPoint(sketch, "E147.bottom.end.orphan", {"position": v(54.8, 465.63) * mm});
            skLineSegment(sketch, "E201.trimOffspring", {"start": v(32.57, 465.63) * mm, "end": v(32.57, 424.36) * mm, "construction": true});
            skPoint(sketch, "E202.orphan", {"position": v(0.82, 475.16) * mm});
            skPoint(sketch, "E203.orphan", {"position": v(64.32, 475.16) * mm});
            skSolve(sketch);
        }
        {
            var Q0;
            {var subQ5=sQuery(id+"F10.wireOp",EDGE,"E147.top");Q0=makeQuery(id+"F10.imprint","IMPRINT",FACE,{"disambiguationData":[TD([[makeQuery(id+"F10.imprint","IMPRINT",EDGE,{"derivedFrom":subQ5}),-1.0]])]});}
            var Q1;
            Q1=makeQuery(id+"F10.imprint","IMPRINT",FACE,{"disambiguationData":[TD([[makeQuery(id+"F10.imprint","IMPRINT",EDGE,{"derivedFrom":sQuery(id+"F10.wireOp",EDGE,"E154.MirrorCS")}),1.0]])]});
            var Q2;
            Q2=makeQuery(id+"F10.imprint","IMPRINT",FACE,{"disambiguationData":[TD([[makeQuery(id+"F10.imprint","IMPRINT",EDGE,{"derivedFrom":sQuery(id+"F10.wireOp",EDGE,"E147.top")}),1.0]])]});
            extrude(context, id + "F11", {"entities" : qUnion([Q0, Q1, Q2]), "depth" : 11.9 * mm});
        }
        {
            var Q0;
            Q0=qCreatedBy(makeId("Top.planeOp"),FACE);
            var sketch = newSketch(context, id + "F12", { "sketchPlane" : qUnion([Q0])});
            skPoint(sketch, "E204.visualSharp", {"position": v(406.26, 947.73) * mm});
            skPoint(sketch, "E205.visualSharp", {"position": v(229.45, 506.82) * mm});
            skLineSegment(sketch, "E206", {"start": v(32.6, 506.82) * mm, "end": v(32.6, 860.3) * mm, "construction": true});
            skLineSegment(sketch, "E207", {"start": v(32.6, 506.82) * mm, "end": v(32.6, 438.24) * mm, "construction": true});
            skLineSegment(sketch, "E208.top", {"start": v(32.6, 628.1) * mm, "end": v(64.35, 628.1) * mm});
            skLineSegment(sketch, "E208.left", {"start": v(32.6, 472.53) * mm, "end": v(32.6, 628.1) * mm});
            skLineSegment(sketch, "E208.right", {"start": v(64.35, 513.8) * mm, "end": v(64.35, 628.1) * mm});
            skLineSegment(sketch, "E209.bottom", {"start": v(64.35, 628.1) * mm, "end": v(89.75, 628.1) * mm});
            skLineSegment(sketch, "E209.top", {"start": v(64.35, 513.8) * mm, "end": v(89.75, 513.8) * mm});
            skLineSegment(sketch, "E209.left", {"start": v(64.35, 628.1) * mm, "end": v(64.35, 513.8) * mm});
            skLineSegment(sketch, "E209.right", {"start": v(89.75, 628.1) * mm, "end": v(89.75, 513.8) * mm});
            skLineSegment(sketch, "E210.bottom", {"start": v(32.6, 513.8) * mm, "end": v(41.98, 513.8) * mm});
            skLineSegment(sketch, "E210.left", {"start": v(32.6, 506.82) * mm, "end": v(32.6, 481.42) * mm});
            skArc(sketch, "E211", {"start": v(70.7, 628.1) * mm, "mid": v(67.52, 631.28) * mm, "end": v(64.35, 628.1) * mm});
            skPoint(sketch, "E212.visualSharp", {"position": v(45.3, 488.4) * mm});
            skLineSegment(sketch, "E212.filletArc", {"start": v(-439.49, 106.29) * mm, "end": v(-439.49, 106.29) * mm});
            skPoint(sketch, "E213.visualSharp", {"position": v(45.3, 513.8) * mm});
            skPoint(sketch, "E214.visualSharp", {"position": v(64.35, 472.53) * mm});
            skArc(sketch, "E214.filletArc", {"start": v(54.82, 482.33) * mm, "mid": v(61.56, 485.12) * mm, "end": v(64.35, 491.86) * mm});
            skArc(sketch, "E215.MirrorCS", {"start": v(19.9, 510.5) * mm, "mid": v(20.87, 512.84) * mm, "end": v(23.2, 513.8) * mm});
            skLineSegment(sketch, "E216.MirrorCS", {"start": v(32.6, 513.8) * mm, "end": v(23.2, 513.8) * mm});
            skLineSegment(sketch, "E217.MirrorCS", {"start": v(-464.89, 106.29) * mm, "end": v(-464.89, 106.29) * mm});
            skArc(sketch, "E218.MirrorCS", {"start": v(-5.5, 628.1) * mm, "mid": v(-2.33, 631.28) * mm, "end": v(0.85, 628.1) * mm});
            skLineSegment(sketch, "E219.MirrorCS", {"start": v(0.85, 628.1) * mm, "end": v(-24.55, 628.1) * mm});
            skLineSegment(sketch, "E220.MirrorCS", {"start": v(0.85, 628.1) * mm, "end": v(0.85, 513.8) * mm});
            skLineSegment(sketch, "E221.MirrorCS", {"start": v(0.85, 513.8) * mm, "end": v(-24.55, 513.8) * mm});
            skPoint(sketch, "E222.MirrorP", {"position": v(19.9, 513.8) * mm});
            skLineSegment(sketch, "E223.MirrorCS", {"start": v(32.6, 628.1) * mm, "end": v(0.85, 628.1) * mm});
            skPoint(sketch, "E224.MirrorP", {"position": v(0.85, 472.53) * mm});
            skLineSegment(sketch, "E225.MirrorCS", {"start": v(0.85, 491.86) * mm, "end": v(0.85, 628.1) * mm});
            skPoint(sketch, "E226.MirrorP", {"position": v(19.9, 488.4) * mm});
            skLineSegment(sketch, "E227.MirrorCS", {"start": v(-24.55, 628.1) * mm, "end": v(-24.55, 513.8) * mm});
            skArc(sketch, "E228.MirrorCS", {"start": v(45.3, 510.5) * mm, "mid": v(44.33, 512.84) * mm, "end": v(41.98, 513.8) * mm});
            skArc(sketch, "E229.MirrorCS", {"start": v(10.37, 482.33) * mm, "mid": v(3.64, 485.12) * mm, "end": v(0.85, 491.86) * mm});
            skLineSegment(sketch, "E230.MirrorCS", {"start": v(32.6, 482.33) * mm, "end": v(54.82, 482.33) * mm});
            skLineSegment(sketch, "E231.MirrorCS", {"start": v(32.6, 482.33) * mm, "end": v(10.37, 482.33) * mm});
            skFitSpline(sketch, "E232", {"points": [v(89.75, 513.8) * mm, v(96.62, 513.8) * mm, v(106.37, 516.65) * mm, v(120.9, 535.75) * mm, v(134, 548.85) * mm, v(171.07, 562.86) * mm, v(208.12, 583.65) * mm, v(239.76, 608.96) * mm, v(300.32, 620.26) * mm, v(374.4, 627.38) * mm, v(406.26, 758.7) * mm], "startDerivative": vector(133.06, -25.03) * mm, "endDerivative": vector(-44.6, 1613.14) * mm});
            skLineSegment(sketch, "E233.MirrorCS", {"start": v(127.85, 947.73) * mm, "end": v(-62.65, 947.73) * mm});
            skPoint(sketch, "E234.MirrorP", {"position": v(-341.07, 947.73) * mm});
            skPoint(sketch, "E235.MirrorP", {"position": v(-164.25, 506.82) * mm});
            skArc(sketch, "E236", {"start": v(89.75, 628.1) * mm, "mid": v(86.57, 631.28) * mm, "end": v(83.4, 628.1) * mm});
            skArc(sketch, "E237", {"start": v(-18.2, 628.1) * mm, "mid": v(-21.38, 631.28) * mm, "end": v(-24.55, 628.1) * mm});
            skLineSegment(sketch, "E238", {"start": v(19.9, 510.5) * mm, "end": v(19.9, 498.07) * mm});
            skLineSegment(sketch, "E239", {"start": v(23.07, 494.9) * mm, "end": v(42.12, 494.9) * mm});
            skLineSegment(sketch, "E240", {"start": v(45.3, 498.07) * mm, "end": v(45.3, 510.5) * mm});
            skPoint(sketch, "E241.visualSharp", {"position": v(19.9, 485.1) * mm});
            skArc(sketch, "E241.filletArc", {"start": v(19.9, 498.07) * mm, "mid": v(20.83, 495.83) * mm, "end": v(23.07, 494.9) * mm});
            skPoint(sketch, "E242.visualSharp", {"position": v(45.3, 485.1) * mm});
            skArc(sketch, "E242.filletArc", {"start": v(42.12, 494.9) * mm, "mid": v(44.37, 495.83) * mm, "end": v(45.3, 498.07) * mm});
            skLineSegment(sketch, "E243", {"start": v(64.35, 491.86) * mm, "end": v(64.35, 513.8) * mm});
            skLineSegment(sketch, "E244", {"start": v(406.26, 758.7) * mm, "end": v(406.26, 922.33) * mm});
            skLineSegment(sketch, "E245", {"start": v(127.85, 947.73) * mm, "end": v(380.86, 947.73) * mm});
            skArc(sketch, "E246.filletArc", {"start": v(406.26, 922.33) * mm, "mid": v(398.82, 940.3) * mm, "end": v(380.86, 947.73) * mm});
            skLineSegment(sketch, "E247.bottom", {"start": v(32.6, 909.63) * mm, "end": v(342.76, 909.63) * mm});
            skLineSegment(sketch, "E247.top", {"start": v(32.6, 666.2) * mm, "end": v(342.76, 666.2) * mm});
            skLineSegment(sketch, "E247.left", {"start": v(32.6, 909.63) * mm, "end": v(32.6, 666.2) * mm});
            skLineSegment(sketch, "E247.right", {"start": v(368.16, 884.23) * mm, "end": v(368.16, 691.6) * mm});
            skPoint(sketch, "E248.visualSharp", {"position": v(368.16, 666.2) * mm});
            skArc(sketch, "E248.filletArc", {"start": v(342.76, 666.2) * mm, "mid": v(360.72, 673.64) * mm, "end": v(368.16, 691.6) * mm});
            skPoint(sketch, "E249.visualSharp", {"position": v(368.16, 909.63) * mm});
            skArc(sketch, "E249.filletArc", {"start": v(368.16, 884.23) * mm, "mid": v(360.72, 902.2) * mm, "end": v(342.76, 909.63) * mm});
            skLineSegment(sketch, "E250.MirrorCS", {"start": v(-341.07, 758.7) * mm, "end": v(-341.07, 922.33) * mm});
            skArc(sketch, "E251.MirrorCS", {"start": v(-302.97, 884.23) * mm, "mid": v(-295.53, 902.2) * mm, "end": v(-277.57, 909.63) * mm});
            skPoint(sketch, "E252.MirrorP", {"position": v(-302.97, 666.2) * mm});
            skArc(sketch, "E253.MirrorCS", {"start": v(-277.57, 666.2) * mm, "mid": v(-295.53, 673.64) * mm, "end": v(-302.97, 691.6) * mm});
            skPoint(sketch, "E254.MirrorP", {"position": v(-302.97, 909.63) * mm});
            skLineSegment(sketch, "E255.MirrorCS", {"start": v(-62.65, 947.73) * mm, "end": v(127.85, 947.73) * mm});
            skLineSegment(sketch, "E256.MirrorCS", {"start": v(-302.97, 884.23) * mm, "end": v(-302.97, 691.6) * mm});
            skFitSpline(sketch, "E257.MirrorCS", {"points": [v(-24.55, 513.8) * mm, v(-31.43, 513.8) * mm, v(-41.18, 516.65) * mm, v(-55.71, 535.75) * mm, v(-68.82, 548.85) * mm, v(-105.87, 562.86) * mm, v(-142.93, 583.65) * mm, v(-174.57, 608.96) * mm, v(-235.13, 620.26) * mm, v(-309.2, 627.38) * mm, v(-341.07, 758.7) * mm], "startDerivative": vector(-133.06, -25.03) * mm, "endDerivative": vector(44.6, 1613.14) * mm});
            skLineSegment(sketch, "E258.MirrorCS", {"start": v(32.6, 666.2) * mm, "end": v(-277.57, 666.2) * mm});
            skArc(sketch, "E259.MirrorCS", {"start": v(-341.07, 922.33) * mm, "mid": v(-333.63, 940.3) * mm, "end": v(-315.67, 947.73) * mm});
            skLineSegment(sketch, "E260.MirrorCS", {"start": v(-62.65, 947.73) * mm, "end": v(-315.67, 947.73) * mm});
            skLineSegment(sketch, "E261.MirrorCS", {"start": v(32.6, 909.63) * mm, "end": v(-277.57, 909.63) * mm});
            skLineSegment(sketch, "E262", {"start": v(0.85, 513.8) * mm, "end": v(64.35, 513.8) * mm, "construction": true});
            skPoint(sketch, "E263.orphan", {"position": v(0.85, 482.06) * mm});
            skPoint(sketch, "E264.orphan", {"position": v(64.35, 482.06) * mm});
            skSolve(sketch);
        }
        {
            var Q0;
            {var subQ5=sQuery(id+"F12.wireOp",EDGE,"E208.top");Q0=makeQuery(id+"F12.imprint","IMPRINT",FACE,{"disambiguationData":[TD([[makeQuery(id+"F12.imprint","IMPRINT",EDGE,{"derivedFrom":subQ5}),-1.0]])]});}
            var Q1;
            Q1=makeQuery(id+"F12.imprint","IMPRINT",FACE,{"disambiguationData":[TD([[makeQuery(id+"F12.imprint","IMPRINT",EDGE,{"derivedFrom":sQuery(id+"F12.wireOp",EDGE,"d7ea122c-9ec8-4e4a-8ab8-e34f7a07d9ba.MirrorCS")}),1.0]])]});
            var Q2;
            Q2=makeQuery(id+"F12.imprint","IMPRINT",FACE,{"disambiguationData":[TD([[makeQuery(id+"F12.imprint","IMPRINT",EDGE,{"derivedFrom":sQuery(id+"F12.wireOp",EDGE,"E208.top")}),1.0]])]});
            var Q3;
            Q3=makeQuery(id+"F12.imprint","IMPRINT",FACE,{"disambiguationData":[TD([[makeQuery(id+"F12.imprint","IMPRINT",EDGE,{"derivedFrom":sQuery(id+"F12.wireOp",EDGE,"E215.MirrorCS")}),1.0]])]});
            extrude(context, id + "F13", {"entities" : qUnion([Q0, Q1, Q2, Q3]), "depth" : 11.9 * mm});
        }
        {
            var Q0;
            Q0=qCreatedBy(makeId("Front.planeOp"),FACE);
            var sketch = newSketch(context, id + "F14", { "sketchPlane" : qUnion([Q0])});
            skLineSegment(sketch, "E265.bottom", {"start": v(-29.21, 112.4) * mm, "end": v(-6.35, 112.4) * mm});
            skLineSegment(sketch, "E265.top", {"start": v(-26.04, 61.6) * mm, "end": v(-9.52, 61.6) * mm});
            skLineSegment(sketch, "E265.left", {"start": v(-29.21, 112.4) * mm, "end": v(-29.21, 64.78) * mm});
            skLineSegment(sketch, "E265.right", {"start": v(-6.35, 112.4) * mm, "end": v(-6.35, 64.78) * mm});
            skLineSegment(sketch, "E266.bottom", {"start": v(10.8, 125.1) * mm, "end": v(-46.36, 125.1) * mm});
            skLineSegment(sketch, "E266.top", {"start": v(13.97, 112.4) * mm, "end": v(0, 112.4) * mm});
            skLineSegment(sketch, "E266.left", {"start": v(13.97, 121.93) * mm, "end": v(13.97, 112.4) * mm});
            skLineSegment(sketch, "E266.right", {"start": v(-49.53, 121.93) * mm, "end": v(-49.53, 112.4) * mm});
            skPoint(sketch, "E267", {"position": v(-5.08, 121.93) * mm});
            skArc(sketch, "E268", {"start": v(0, 112.4) * mm, "mid": v(-3.17, 115.58) * mm, "end": v(-6.35, 112.4) * mm});
            skArc(sketch, "E269", {"start": v(-29.2, 112.4) * mm, "mid": v(-32.38, 115.58) * mm, "end": v(-35.56, 112.4) * mm});
            skPoint(sketch, "E270.visualSharp", {"position": v(-49.53, 121.93) * mm});
            skArc(sketch, "E270.filletArc", {"start": v(-46.36, 125.1) * mm, "mid": v(-48.6, 124.17) * mm, "end": v(-49.53, 121.93) * mm});
            skPoint(sketch, "E271.visualSharp", {"position": v(13.97, 125.1) * mm});
            skArc(sketch, "E271.filletArc", {"start": v(13.97, 121.93) * mm, "mid": v(13.04, 124.17) * mm, "end": v(10.8, 125.1) * mm});
            skPoint(sketch, "E272.visualSharp", {"position": v(-6.35, 61.6) * mm});
            skArc(sketch, "E272.filletArc", {"start": v(-9.52, 61.6) * mm, "mid": v(-7.28, 62.53) * mm, "end": v(-6.35, 64.78) * mm});
            skPoint(sketch, "E273.visualSharp", {"position": v(-29.21, 61.6) * mm});
            skArc(sketch, "E273.filletArc", {"start": v(-29.21, 64.78) * mm, "mid": v(-28.28, 62.53) * mm, "end": v(-26.04, 61.6) * mm});
            skLineSegment(sketch, "E274.trimOffspring", {"start": v(-35.56, 112.4) * mm, "end": v(-49.53, 112.4) * mm});
            skLineSegment(sketch, "E275.trimOffspring", {"start": v(-6.35, 112.4) * mm, "end": v(-29.21, 112.4) * mm});
            skSolve(sketch);
        }
        {
            var Q0;
            Q0 = qSketchRegion(id + "F14", true);
            extrude(context, id + "F15", {"entities" : qUnion([Q0]), "depth" : 18.77 * mm});
        }
        {
            var Q0;
            Q0=qCreatedBy(makeId("Front.planeOp"),FACE);
            var sketch = newSketch(context, id + "F16", { "sketchPlane" : qUnion([Q0])});
            skLineSegment(sketch, "E276.bottom", {"start": v(68.42, 663.27) * mm, "end": v(170.78, 663.27) * mm});
            skLineSegment(sketch, "E276.top", {"start": v(68.42, -505.13) * mm, "end": v(170.78, -505.13) * mm});
            skLineSegment(sketch, "E276.left", {"start": v(68.42, 663.27) * mm, "end": v(68.42, -505.13) * mm});
            skLineSegment(sketch, "E276.right", {"start": v(170.78, 663.27) * mm, "end": v(170.78, -505.13) * mm});
            skLineSegment(sketch, "E277.bottom", {"start": v(90.64, -474.4) * mm, "end": v(160.5, -474.4) * mm});
            skLineSegment(sketch, "E277.top", {"start": v(90.64, -486.08) * mm, "end": v(160.5, -486.08) * mm});
            skLineSegment(sketch, "E277.left", {"start": v(90.64, -474.4) * mm, "end": v(90.64, -486.08) * mm});
            skLineSegment(sketch, "E277.right", {"start": v(160.5, -474.4) * mm, "end": v(160.5, -486.08) * mm});
            skLineSegment(sketch, "E278", {"start": v(119.6, -505.13) * mm, "end": v(119.6, -373.16) * mm, "construction": true});
            skLineSegment(sketch, "E279", {"start": v(68.42, -346.92) * mm, "end": v(182.72, -346.92) * mm, "construction": true});
            skLineSegment(sketch, "E280", {"start": v(125.57, -346.92) * mm, "end": v(125.57, -534.23) * mm, "construction": true});
            skLineSegment(sketch, "E281.0.1.0", {"start": v(160.5, -372.8) * mm, "end": v(160.5, -384.48) * mm});
            skLineSegment(sketch, "E281.0.1.1", {"start": v(90.64, -384.48) * mm, "end": v(160.5, -384.48) * mm});
            skLineSegment(sketch, "E281.0.1.2", {"start": v(90.64, -372.8) * mm, "end": v(160.5, -372.8) * mm});
            skLineSegment(sketch, "E281.0.1.3", {"start": v(90.64, -372.8) * mm, "end": v(90.64, -384.48) * mm});
            skLineSegment(sketch, "E281.0.2.0", {"start": v(160.5, -271.2) * mm, "end": v(160.5, -282.88) * mm});
            skLineSegment(sketch, "E281.0.2.1", {"start": v(90.64, -282.88) * mm, "end": v(160.5, -282.88) * mm});
            skLineSegment(sketch, "E281.0.2.2", {"start": v(90.64, -271.2) * mm, "end": v(160.5, -271.2) * mm});
            skLineSegment(sketch, "E281.0.2.3", {"start": v(90.64, -271.2) * mm, "end": v(90.64, -282.88) * mm});
            skLineSegment(sketch, "E281.0.3.0", {"start": v(160.5, -169.6) * mm, "end": v(160.5, -181.28) * mm});
            skLineSegment(sketch, "E281.0.3.1", {"start": v(90.64, -181.28) * mm, "end": v(160.5, -181.28) * mm});
            skLineSegment(sketch, "E281.0.3.2", {"start": v(90.64, -169.6) * mm, "end": v(160.5, -169.6) * mm});
            skLineSegment(sketch, "E281.0.3.3", {"start": v(90.64, -169.6) * mm, "end": v(90.64, -181.28) * mm});
            skLineSegment(sketch, "E281.0.4.0", {"start": v(160.5, -68) * mm, "end": v(160.5, -79.68) * mm});
            skLineSegment(sketch, "E281.0.4.1", {"start": v(90.64, -79.68) * mm, "end": v(160.5, -79.68) * mm});
            skLineSegment(sketch, "E281.0.4.2", {"start": v(90.64, -68) * mm, "end": v(160.5, -68) * mm});
            skLineSegment(sketch, "E281.0.4.3", {"start": v(90.64, -68) * mm, "end": v(90.64, -79.68) * mm});
            skLineSegment(sketch, "E281.0.5.0", {"start": v(160.5, 33.6) * mm, "end": v(160.5, 21.92) * mm});
            skLineSegment(sketch, "E281.0.5.1", {"start": v(90.64, 21.92) * mm, "end": v(160.5, 21.92) * mm});
            skLineSegment(sketch, "E281.0.5.2", {"start": v(90.64, 33.6) * mm, "end": v(160.5, 33.6) * mm});
            skLineSegment(sketch, "E281.0.5.3", {"start": v(90.64, 33.6) * mm, "end": v(90.64, 21.92) * mm});
            skLineSegment(sketch, "E281.0.6.0", {"start": v(160.5, 135.2) * mm, "end": v(160.5, 123.52) * mm});
            skLineSegment(sketch, "E281.0.6.1", {"start": v(90.64, 123.52) * mm, "end": v(160.5, 123.52) * mm});
            skLineSegment(sketch, "E281.0.6.2", {"start": v(90.64, 135.2) * mm, "end": v(160.5, 135.2) * mm});
            skLineSegment(sketch, "E281.0.6.3", {"start": v(90.64, 135.2) * mm, "end": v(90.64, 123.52) * mm});
            skLineSegment(sketch, "E281.0.7.0", {"start": v(160.5, 236.8) * mm, "end": v(160.5, 225.12) * mm});
            skLineSegment(sketch, "E281.0.7.1", {"start": v(90.64, 225.12) * mm, "end": v(160.5, 225.12) * mm});
            skLineSegment(sketch, "E281.0.7.2", {"start": v(90.64, 236.8) * mm, "end": v(160.5, 236.8) * mm});
            skLineSegment(sketch, "E281.0.7.3", {"start": v(90.64, 236.8) * mm, "end": v(90.64, 225.12) * mm});
            skLineSegment(sketch, "E281.0.8.0", {"start": v(160.5, 338.4) * mm, "end": v(160.5, 326.72) * mm});
            skLineSegment(sketch, "E281.0.8.1", {"start": v(90.64, 326.72) * mm, "end": v(160.5, 326.72) * mm});
            skLineSegment(sketch, "E281.0.8.2", {"start": v(90.64, 338.4) * mm, "end": v(160.5, 338.4) * mm});
            skLineSegment(sketch, "E281.0.8.3", {"start": v(90.64, 338.4) * mm, "end": v(90.64, 326.72) * mm});
            skLineSegment(sketch, "E281.0.9.0", {"start": v(160.5, 440) * mm, "end": v(160.5, 428.32) * mm});
            skLineSegment(sketch, "E281.0.9.1", {"start": v(90.64, 428.32) * mm, "end": v(160.5, 428.32) * mm});
            skLineSegment(sketch, "E281.0.9.2", {"start": v(90.64, 440) * mm, "end": v(160.5, 440) * mm});
            skLineSegment(sketch, "E281.0.9.3", {"start": v(90.64, 440) * mm, "end": v(90.64, 428.32) * mm});
            skLineSegment(sketch, "E281.0.10.0", {"start": v(160.5, 541.6) * mm, "end": v(160.5, 529.92) * mm});
            skLineSegment(sketch, "E281.0.10.1", {"start": v(90.64, 529.92) * mm, "end": v(160.5, 529.92) * mm});
            skLineSegment(sketch, "E281.0.10.2", {"start": v(90.64, 541.6) * mm, "end": v(160.5, 541.6) * mm});
            skLineSegment(sketch, "E281.0.10.3", {"start": v(90.64, 541.6) * mm, "end": v(90.64, 529.92) * mm});
            skLineSegment(sketch, "E281.0.11.0", {"start": v(160.5, 643.2) * mm, "end": v(160.5, 631.52) * mm});
            skLineSegment(sketch, "E281.0.11.1", {"start": v(90.64, 631.52) * mm, "end": v(160.5, 631.52) * mm});
            skLineSegment(sketch, "E281.0.11.2", {"start": v(90.64, 643.2) * mm, "end": v(160.5, 643.2) * mm});
            skLineSegment(sketch, "E281.0.11.3", {"start": v(90.64, 643.2) * mm, "end": v(90.64, 631.52) * mm});
            skLineSegment(sketch, "E281.direction1", {"start": v(90.64, -486.08) * mm, "end": v(116.04, -486.08) * mm, "construction": true});
            skLineSegment(sketch, "E281.direction2", {"start": v(90.64, -486.08) * mm, "end": v(90.64, -384.48) * mm, "construction": true});
            skLineSegment(sketch, "E282.bottom", {"start": v(729.87, 922.14) * mm, "end": v(820.9, 922.14) * mm});
            skLineSegment(sketch, "E282.top", {"start": v(729.87, -246.26) * mm, "end": v(820.9, -246.26) * mm});
            skLineSegment(sketch, "E282.left", {"start": v(729.87, 922.14) * mm, "end": v(729.87, -246.26) * mm});
            skLineSegment(sketch, "E282.right", {"start": v(820.9, 922.14) * mm, "end": v(820.9, -246.26) * mm});
            skLineSegment(sketch, "E283.bottom", {"start": v(740.46, -215.53) * mm, "end": v(810.31, -215.53) * mm});
            skLineSegment(sketch, "E283.top", {"start": v(740.46, -227.21) * mm, "end": v(810.31, -227.21) * mm});
            skLineSegment(sketch, "E283.left", {"start": v(740.46, -215.53) * mm, "end": v(740.46, -227.21) * mm});
            skLineSegment(sketch, "E283.right", {"start": v(810.31, -215.53) * mm, "end": v(810.31, -227.21) * mm});
            skLineSegment(sketch, "E284.direction1", {"start": v(740.46, -227.21) * mm, "end": v(777.5, -227.21) * mm, "construction": true});
            skLineSegment(sketch, "E285.0.1.0", {"start": v(740.46, -113.93) * mm, "end": v(810.31, -113.93) * mm});
            skLineSegment(sketch, "E285.0.1.1", {"start": v(810.31, -113.93) * mm, "end": v(810.31, -125.61) * mm});
            skLineSegment(sketch, "E285.0.1.2", {"start": v(740.46, -125.61) * mm, "end": v(810.31, -125.61) * mm});
            skLineSegment(sketch, "E285.0.1.3", {"start": v(740.46, -113.93) * mm, "end": v(740.46, -125.61) * mm});
            skLineSegment(sketch, "E285.0.2.0", {"start": v(740.46, -12.33) * mm, "end": v(810.31, -12.33) * mm});
            skLineSegment(sketch, "E285.0.2.1", {"start": v(810.31, -12.33) * mm, "end": v(810.31, -24.01) * mm});
            skLineSegment(sketch, "E285.0.2.2", {"start": v(740.46, -24.01) * mm, "end": v(810.31, -24.01) * mm});
            skLineSegment(sketch, "E285.0.2.3", {"start": v(740.46, -12.33) * mm, "end": v(740.46, -24.01) * mm});
            skLineSegment(sketch, "E285.0.3.0", {"start": v(740.46, 89.27) * mm, "end": v(810.31, 89.27) * mm});
            skLineSegment(sketch, "E285.0.3.1", {"start": v(810.31, 89.27) * mm, "end": v(810.31, 77.59) * mm});
            skLineSegment(sketch, "E285.0.3.2", {"start": v(740.46, 77.59) * mm, "end": v(810.31, 77.59) * mm});
            skLineSegment(sketch, "E285.0.3.3", {"start": v(740.46, 89.27) * mm, "end": v(740.46, 77.59) * mm});
            skLineSegment(sketch, "E285.0.4.0", {"start": v(740.46, 190.87) * mm, "end": v(810.31, 190.87) * mm});
            skLineSegment(sketch, "E285.0.4.1", {"start": v(810.31, 190.87) * mm, "end": v(810.31, 179.19) * mm});
            skLineSegment(sketch, "E285.0.4.2", {"start": v(740.46, 179.19) * mm, "end": v(810.31, 179.19) * mm});
            skLineSegment(sketch, "E285.0.4.3", {"start": v(740.46, 190.87) * mm, "end": v(740.46, 179.19) * mm});
            skLineSegment(sketch, "E285.0.5.0", {"start": v(740.46, 292.47) * mm, "end": v(810.31, 292.47) * mm});
            skLineSegment(sketch, "E285.0.5.1", {"start": v(810.31, 292.47) * mm, "end": v(810.31, 280.79) * mm});
            skLineSegment(sketch, "E285.0.5.2", {"start": v(740.46, 280.79) * mm, "end": v(810.31, 280.79) * mm});
            skLineSegment(sketch, "E285.0.5.3", {"start": v(740.46, 292.47) * mm, "end": v(740.46, 280.79) * mm});
            skLineSegment(sketch, "E285.0.6.0", {"start": v(740.46, 394.07) * mm, "end": v(810.31, 394.07) * mm});
            skLineSegment(sketch, "E285.0.6.1", {"start": v(810.31, 394.07) * mm, "end": v(810.31, 382.39) * mm});
            skLineSegment(sketch, "E285.0.6.2", {"start": v(740.46, 382.39) * mm, "end": v(810.31, 382.39) * mm});
            skLineSegment(sketch, "E285.0.6.3", {"start": v(740.46, 394.07) * mm, "end": v(740.46, 382.39) * mm});
            skLineSegment(sketch, "E285.0.7.0", {"start": v(740.46, 495.67) * mm, "end": v(810.31, 495.67) * mm});
            skLineSegment(sketch, "E285.0.7.1", {"start": v(810.31, 495.67) * mm, "end": v(810.31, 483.99) * mm});
            skLineSegment(sketch, "E285.0.7.2", {"start": v(740.46, 483.99) * mm, "end": v(810.31, 483.99) * mm});
            skLineSegment(sketch, "E285.0.7.3", {"start": v(740.46, 495.67) * mm, "end": v(740.46, 483.99) * mm});
            skLineSegment(sketch, "E285.0.8.0", {"start": v(740.46, 597.27) * mm, "end": v(810.31, 597.27) * mm});
            skLineSegment(sketch, "E285.0.8.1", {"start": v(810.31, 597.27) * mm, "end": v(810.31, 585.59) * mm});
            skLineSegment(sketch, "E285.0.8.2", {"start": v(740.46, 585.59) * mm, "end": v(810.31, 585.59) * mm});
            skLineSegment(sketch, "E285.0.8.3", {"start": v(740.46, 597.27) * mm, "end": v(740.46, 585.59) * mm});
            skLineSegment(sketch, "E285.0.9.0", {"start": v(740.46, 698.87) * mm, "end": v(810.31, 698.87) * mm});
            skLineSegment(sketch, "E285.0.9.1", {"start": v(810.31, 698.87) * mm, "end": v(810.31, 687.19) * mm});
            skLineSegment(sketch, "E285.0.9.2", {"start": v(740.46, 687.19) * mm, "end": v(810.31, 687.19) * mm});
            skLineSegment(sketch, "E285.0.9.3", {"start": v(740.46, 698.87) * mm, "end": v(740.46, 687.19) * mm});
            skLineSegment(sketch, "E285.0.10.0", {"start": v(740.46, 800.47) * mm, "end": v(810.31, 800.47) * mm});
            skLineSegment(sketch, "E285.0.10.1", {"start": v(810.31, 800.47) * mm, "end": v(810.31, 788.79) * mm});
            skLineSegment(sketch, "E285.0.10.2", {"start": v(740.46, 788.79) * mm, "end": v(810.31, 788.79) * mm});
            skLineSegment(sketch, "E285.0.10.3", {"start": v(740.46, 800.47) * mm, "end": v(740.46, 788.79) * mm});
            skLineSegment(sketch, "E285.0.11.0", {"start": v(740.46, 902.07) * mm, "end": v(810.31, 902.07) * mm});
            skLineSegment(sketch, "E285.0.11.1", {"start": v(810.31, 902.07) * mm, "end": v(810.31, 890.39) * mm});
            skLineSegment(sketch, "E285.0.11.2", {"start": v(740.46, 890.39) * mm, "end": v(810.31, 890.39) * mm});
            skLineSegment(sketch, "E285.0.11.3", {"start": v(740.46, 902.07) * mm, "end": v(740.46, 890.39) * mm});
            skLineSegment(sketch, "E285.direction1", {"start": v(740.46, -227.21) * mm, "end": v(765.86, -227.21) * mm, "construction": true});
            skLineSegment(sketch, "E285.direction2", {"start": v(740.46, -227.21) * mm, "end": v(740.46, -125.61) * mm, "construction": true});
            skLineSegment(sketch, "E286.bottom", {"start": v(357.06, -448.72) * mm, "end": v(423.1, -448.72) * mm});
            skLineSegment(sketch, "E286.top", {"start": v(357.06, -460.65) * mm, "end": v(423.1, -460.65) * mm});
            skLineSegment(sketch, "E286.left", {"start": v(357.06, -448.72) * mm, "end": v(357.06, -460.65) * mm});
            skLineSegment(sketch, "E286.right", {"start": v(423.1, -448.72) * mm, "end": v(423.1, -460.65) * mm});
            skLineSegment(sketch, "E287.bottom", {"start": v(396.05, -473.35) * mm, "end": v(384.11, -473.35) * mm});
            skLineSegment(sketch, "E287.left", {"start": v(396.05, -473.35) * mm, "end": v(396.05, -460.65) * mm});
            skLineSegment(sketch, "E287.right", {"start": v(384.11, -473.35) * mm, "end": v(384.11, -460.65) * mm});
            skPoint(sketch, "E287.middle", {"position": v(390.08, -460.65) * mm});
            skArc(sketch, "E288", {"start": v(363.41, -448.72) * mm, "mid": v(360.24, -445.54) * mm, "end": v(357.06, -448.72) * mm});
            skArc(sketch, "E289", {"start": v(423.1, -448.72) * mm, "mid": v(419.93, -445.54) * mm, "end": v(416.75, -448.72) * mm});
            skArc(sketch, "E290", {"start": v(416.75, -460.65) * mm, "mid": v(419.93, -463.83) * mm, "end": v(423.1, -460.65) * mm});
            skArc(sketch, "E291", {"start": v(357.06, -460.65) * mm, "mid": v(360.24, -463.83) * mm, "end": v(363.41, -460.65) * mm});
            skArc(sketch, "E292", {"start": v(396.05, -473.35) * mm, "mid": v(399.22, -470.18) * mm, "end": v(396.05, -467) * mm});
            skArc(sketch, "E293", {"start": v(384.11, -467) * mm, "mid": v(380.94, -470.18) * mm, "end": v(384.11, -473.35) * mm});
            skPoint(sketch, "E294.orphan", {"position": v(384.11, -447.95) * mm});
            skPoint(sketch, "E295.orphan", {"position": v(396.05, -447.95) * mm});
            skLineSegment(sketch, "E296.bottom", {"start": v(435.3, -498.75) * mm, "end": v(332.93, -498.75) * mm});
            skLineSegment(sketch, "E296.top", {"start": v(435.3, 707.75) * mm, "end": v(332.93, 707.75) * mm});
            skLineSegment(sketch, "E296.left", {"start": v(435.3, -498.75) * mm, "end": v(435.3, 707.75) * mm});
            skLineSegment(sketch, "E296.right", {"start": v(332.93, -498.75) * mm, "end": v(332.93, 707.75) * mm});
            skPoint(sketch, "E296.middle", {"position": v(384.11, 104.5) * mm});
            skLineSegment(sketch, "E297.0.1.0", {"start": v(357.06, -347.12) * mm, "end": v(357.06, -359.05) * mm});
            skPoint(sketch, "E297.0.1.1", {"position": v(390.08, -359.05) * mm});
            skLineSegment(sketch, "E297.0.1.2", {"start": v(423.1, -347.12) * mm, "end": v(423.1, -359.05) * mm});
            skPoint(sketch, "E297.0.1.3", {"position": v(384.11, -346.35) * mm});
            skLineSegment(sketch, "E297.0.1.4", {"start": v(357.06, -347.12) * mm, "end": v(423.1, -347.12) * mm});
            skLineSegment(sketch, "E297.0.1.5", {"start": v(396.05, -371.75) * mm, "end": v(384.11, -371.75) * mm});
            skPoint(sketch, "E297.0.1.6", {"position": v(396.05, -346.35) * mm});
            skLineSegment(sketch, "E297.0.1.7", {"start": v(357.06, -359.05) * mm, "end": v(423.1, -359.05) * mm});
            skArc(sketch, "E297.0.1.8", {"start": v(423.1, -347.12) * mm, "mid": v(419.93, -343.94) * mm, "end": v(416.75, -347.12) * mm});
            skLineSegment(sketch, "E297.0.1.9", {"start": v(384.11, -371.75) * mm, "end": v(384.11, -359.05) * mm});
            skArc(sketch, "E297.0.1.10", {"start": v(416.75, -359.05) * mm, "mid": v(419.93, -362.23) * mm, "end": v(423.1, -359.05) * mm});
            skArc(sketch, "E297.0.1.11", {"start": v(384.11, -365.4) * mm, "mid": v(380.94, -368.58) * mm, "end": v(384.11, -371.75) * mm});
            skArc(sketch, "E297.0.1.12", {"start": v(357.06, -359.05) * mm, "mid": v(360.24, -362.23) * mm, "end": v(363.41, -359.05) * mm});
            skLineSegment(sketch, "E297.0.1.13", {"start": v(396.05, -371.75) * mm, "end": v(396.05, -359.05) * mm});
            skArc(sketch, "E297.0.1.14", {"start": v(363.41, -347.12) * mm, "mid": v(360.24, -343.94) * mm, "end": v(357.06, -347.12) * mm});
            skArc(sketch, "E297.0.1.15", {"start": v(396.05, -371.75) * mm, "mid": v(399.22, -368.58) * mm, "end": v(396.05, -365.4) * mm});
            skLineSegment(sketch, "E297.0.2.0", {"start": v(357.06, -245.52) * mm, "end": v(357.06, -257.45) * mm});
            skPoint(sketch, "E297.0.2.1", {"position": v(390.08, -257.45) * mm});
            skLineSegment(sketch, "E297.0.2.2", {"start": v(423.1, -245.52) * mm, "end": v(423.1, -257.45) * mm});
            skPoint(sketch, "E297.0.2.3", {"position": v(384.11, -244.75) * mm});
            skLineSegment(sketch, "E297.0.2.4", {"start": v(357.06, -245.52) * mm, "end": v(423.1, -245.52) * mm});
            skLineSegment(sketch, "E297.0.2.5", {"start": v(396.05, -270.15) * mm, "end": v(384.11, -270.15) * mm});
            skPoint(sketch, "E297.0.2.6", {"position": v(396.05, -244.75) * mm});
            skLineSegment(sketch, "E297.0.2.7", {"start": v(357.06, -257.45) * mm, "end": v(423.1, -257.45) * mm});
            skArc(sketch, "E297.0.2.8", {"start": v(423.1, -245.52) * mm, "mid": v(419.93, -242.34) * mm, "end": v(416.75, -245.52) * mm});
            skLineSegment(sketch, "E297.0.2.9", {"start": v(384.11, -270.15) * mm, "end": v(384.11, -257.45) * mm});
            skArc(sketch, "E297.0.2.10", {"start": v(416.75, -257.45) * mm, "mid": v(419.93, -260.63) * mm, "end": v(423.1, -257.45) * mm});
            skArc(sketch, "E297.0.2.11", {"start": v(384.11, -263.8) * mm, "mid": v(380.94, -266.98) * mm, "end": v(384.11, -270.15) * mm});
            skArc(sketch, "E297.0.2.12", {"start": v(357.06, -257.45) * mm, "mid": v(360.24, -260.63) * mm, "end": v(363.41, -257.45) * mm});
            skLineSegment(sketch, "E297.0.2.13", {"start": v(396.05, -270.15) * mm, "end": v(396.05, -257.45) * mm});
            skArc(sketch, "E297.0.2.14", {"start": v(363.41, -245.52) * mm, "mid": v(360.24, -242.34) * mm, "end": v(357.06, -245.52) * mm});
            skArc(sketch, "E297.0.2.15", {"start": v(396.05, -270.15) * mm, "mid": v(399.22, -266.98) * mm, "end": v(396.05, -263.8) * mm});
            skLineSegment(sketch, "E297.0.3.0", {"start": v(357.06, -143.92) * mm, "end": v(357.06, -155.85) * mm});
            skPoint(sketch, "E297.0.3.1", {"position": v(390.08, -155.85) * mm});
            skLineSegment(sketch, "E297.0.3.2", {"start": v(423.1, -143.92) * mm, "end": v(423.1, -155.85) * mm});
            skPoint(sketch, "E297.0.3.3", {"position": v(384.11, -143.15) * mm});
            skLineSegment(sketch, "E297.0.3.4", {"start": v(357.06, -143.92) * mm, "end": v(423.1, -143.92) * mm});
            skLineSegment(sketch, "E297.0.3.5", {"start": v(396.05, -168.55) * mm, "end": v(384.11, -168.55) * mm});
            skPoint(sketch, "E297.0.3.6", {"position": v(396.05, -143.15) * mm});
            skLineSegment(sketch, "E297.0.3.7", {"start": v(357.06, -155.85) * mm, "end": v(423.1, -155.85) * mm});
            skArc(sketch, "E297.0.3.8", {"start": v(423.1, -143.92) * mm, "mid": v(419.93, -140.74) * mm, "end": v(416.75, -143.92) * mm});
            skLineSegment(sketch, "E297.0.3.9", {"start": v(384.11, -168.55) * mm, "end": v(384.11, -155.85) * mm});
            skArc(sketch, "E297.0.3.10", {"start": v(416.75, -155.85) * mm, "mid": v(419.93, -159.03) * mm, "end": v(423.1, -155.85) * mm});
            skArc(sketch, "E297.0.3.11", {"start": v(384.11, -162.2) * mm, "mid": v(380.94, -165.38) * mm, "end": v(384.11, -168.55) * mm});
            skArc(sketch, "E297.0.3.12", {"start": v(357.06, -155.85) * mm, "mid": v(360.24, -159.03) * mm, "end": v(363.41, -155.85) * mm});
            skLineSegment(sketch, "E297.0.3.13", {"start": v(396.05, -168.55) * mm, "end": v(396.05, -155.85) * mm});
            skArc(sketch, "E297.0.3.14", {"start": v(363.41, -143.92) * mm, "mid": v(360.24, -140.74) * mm, "end": v(357.06, -143.92) * mm});
            skArc(sketch, "E297.0.3.15", {"start": v(396.05, -168.55) * mm, "mid": v(399.22, -165.38) * mm, "end": v(396.05, -162.2) * mm});
            skLineSegment(sketch, "E297.0.4.0", {"start": v(357.06, -42.32) * mm, "end": v(357.06, -54.25) * mm});
            skPoint(sketch, "E297.0.4.1", {"position": v(390.08, -54.25) * mm});
            skLineSegment(sketch, "E297.0.4.2", {"start": v(423.1, -42.32) * mm, "end": v(423.1, -54.25) * mm});
            skPoint(sketch, "E297.0.4.3", {"position": v(384.11, -41.55) * mm});
            skLineSegment(sketch, "E297.0.4.4", {"start": v(357.06, -42.32) * mm, "end": v(423.1, -42.32) * mm});
            skLineSegment(sketch, "E297.0.4.5", {"start": v(396.05, -66.95) * mm, "end": v(384.11, -66.95) * mm});
            skPoint(sketch, "E297.0.4.6", {"position": v(396.05, -41.55) * mm});
            skLineSegment(sketch, "E297.0.4.7", {"start": v(357.06, -54.25) * mm, "end": v(423.1, -54.25) * mm});
            skArc(sketch, "E297.0.4.8", {"start": v(423.1, -42.32) * mm, "mid": v(419.93, -39.14) * mm, "end": v(416.75, -42.32) * mm});
            skLineSegment(sketch, "E297.0.4.9", {"start": v(384.11, -66.95) * mm, "end": v(384.11, -54.25) * mm});
            skArc(sketch, "E297.0.4.10", {"start": v(416.75, -54.25) * mm, "mid": v(419.93, -57.43) * mm, "end": v(423.1, -54.25) * mm});
            skArc(sketch, "E297.0.4.11", {"start": v(384.11, -60.6) * mm, "mid": v(380.94, -63.78) * mm, "end": v(384.11, -66.95) * mm});
            skArc(sketch, "E297.0.4.12", {"start": v(357.06, -54.25) * mm, "mid": v(360.24, -57.43) * mm, "end": v(363.41, -54.25) * mm});
            skLineSegment(sketch, "E297.0.4.13", {"start": v(396.05, -66.95) * mm, "end": v(396.05, -54.25) * mm});
            skArc(sketch, "E297.0.4.14", {"start": v(363.41, -42.32) * mm, "mid": v(360.24, -39.14) * mm, "end": v(357.06, -42.32) * mm});
            skArc(sketch, "E297.0.4.15", {"start": v(396.05, -66.95) * mm, "mid": v(399.22, -63.78) * mm, "end": v(396.05, -60.6) * mm});
            skLineSegment(sketch, "E297.0.5.0", {"start": v(357.06, 59.28) * mm, "end": v(357.06, 47.35) * mm});
            skPoint(sketch, "E297.0.5.1", {"position": v(390.08, 47.35) * mm});
            skLineSegment(sketch, "E297.0.5.2", {"start": v(423.1, 59.28) * mm, "end": v(423.1, 47.35) * mm});
            skPoint(sketch, "E297.0.5.3", {"position": v(384.11, 60.05) * mm});
            skLineSegment(sketch, "E297.0.5.4", {"start": v(357.06, 59.28) * mm, "end": v(423.1, 59.28) * mm});
            skLineSegment(sketch, "E297.0.5.5", {"start": v(396.05, 34.65) * mm, "end": v(384.11, 34.65) * mm});
            skPoint(sketch, "E297.0.5.6", {"position": v(396.05, 60.05) * mm});
            skLineSegment(sketch, "E297.0.5.7", {"start": v(357.06, 47.35) * mm, "end": v(423.1, 47.35) * mm});
            skArc(sketch, "E297.0.5.8", {"start": v(423.1, 59.28) * mm, "mid": v(419.93, 62.46) * mm, "end": v(416.75, 59.28) * mm});
            skLineSegment(sketch, "E297.0.5.9", {"start": v(384.11, 34.65) * mm, "end": v(384.11, 47.35) * mm});
            skArc(sketch, "E297.0.5.10", {"start": v(416.75, 47.35) * mm, "mid": v(419.93, 44.17) * mm, "end": v(423.1, 47.35) * mm});
            skArc(sketch, "E297.0.5.11", {"start": v(384.11, 41) * mm, "mid": v(380.94, 37.82) * mm, "end": v(384.11, 34.65) * mm});
            skArc(sketch, "E297.0.5.12", {"start": v(357.06, 47.35) * mm, "mid": v(360.24, 44.17) * mm, "end": v(363.41, 47.35) * mm});
            skLineSegment(sketch, "E297.0.5.13", {"start": v(396.05, 34.65) * mm, "end": v(396.05, 47.35) * mm});
            skArc(sketch, "E297.0.5.14", {"start": v(363.41, 59.28) * mm, "mid": v(360.24, 62.46) * mm, "end": v(357.06, 59.28) * mm});
            skArc(sketch, "E297.0.5.15", {"start": v(396.05, 34.65) * mm, "mid": v(399.22, 37.82) * mm, "end": v(396.05, 41) * mm});
            skLineSegment(sketch, "E297.0.6.0", {"start": v(357.06, 160.88) * mm, "end": v(357.06, 148.95) * mm});
            skPoint(sketch, "E297.0.6.1", {"position": v(390.08, 148.95) * mm});
            skLineSegment(sketch, "E297.0.6.2", {"start": v(423.1, 160.88) * mm, "end": v(423.1, 148.95) * mm});
            skPoint(sketch, "E297.0.6.3", {"position": v(384.11, 161.65) * mm});
            skLineSegment(sketch, "E297.0.6.4", {"start": v(357.06, 160.88) * mm, "end": v(423.1, 160.88) * mm});
            skLineSegment(sketch, "E297.0.6.5", {"start": v(396.05, 136.25) * mm, "end": v(384.11, 136.25) * mm});
            skPoint(sketch, "E297.0.6.6", {"position": v(396.05, 161.65) * mm});
            skLineSegment(sketch, "E297.0.6.7", {"start": v(357.06, 148.95) * mm, "end": v(423.1, 148.95) * mm});
            skArc(sketch, "E297.0.6.8", {"start": v(423.1, 160.88) * mm, "mid": v(419.93, 164.06) * mm, "end": v(416.75, 160.88) * mm});
            skLineSegment(sketch, "E297.0.6.9", {"start": v(384.11, 136.25) * mm, "end": v(384.11, 148.95) * mm});
            skArc(sketch, "E297.0.6.10", {"start": v(416.75, 148.95) * mm, "mid": v(419.93, 145.77) * mm, "end": v(423.1, 148.95) * mm});
            skArc(sketch, "E297.0.6.11", {"start": v(384.11, 142.6) * mm, "mid": v(380.94, 139.42) * mm, "end": v(384.11, 136.25) * mm});
            skArc(sketch, "E297.0.6.12", {"start": v(357.06, 148.95) * mm, "mid": v(360.24, 145.77) * mm, "end": v(363.41, 148.95) * mm});
            skLineSegment(sketch, "E297.0.6.13", {"start": v(396.05, 136.25) * mm, "end": v(396.05, 148.95) * mm});
            skArc(sketch, "E297.0.6.14", {"start": v(363.41, 160.88) * mm, "mid": v(360.24, 164.06) * mm, "end": v(357.06, 160.88) * mm});
            skArc(sketch, "E297.0.6.15", {"start": v(396.05, 136.25) * mm, "mid": v(399.22, 139.42) * mm, "end": v(396.05, 142.6) * mm});
            skLineSegment(sketch, "E297.0.7.0", {"start": v(357.06, 262.48) * mm, "end": v(357.06, 250.55) * mm});
            skPoint(sketch, "E297.0.7.1", {"position": v(390.08, 250.55) * mm});
            skLineSegment(sketch, "E297.0.7.2", {"start": v(423.1, 262.48) * mm, "end": v(423.1, 250.55) * mm});
            skPoint(sketch, "E297.0.7.3", {"position": v(384.11, 263.25) * mm});
            skLineSegment(sketch, "E297.0.7.4", {"start": v(357.06, 262.48) * mm, "end": v(423.1, 262.48) * mm});
            skLineSegment(sketch, "E297.0.7.5", {"start": v(396.05, 237.85) * mm, "end": v(384.11, 237.85) * mm});
            skPoint(sketch, "E297.0.7.6", {"position": v(396.05, 263.25) * mm});
            skLineSegment(sketch, "E297.0.7.7", {"start": v(357.06, 250.55) * mm, "end": v(423.1, 250.55) * mm});
            skArc(sketch, "E297.0.7.8", {"start": v(423.1, 262.48) * mm, "mid": v(419.93, 265.66) * mm, "end": v(416.75, 262.48) * mm});
            skLineSegment(sketch, "E297.0.7.9", {"start": v(384.11, 237.85) * mm, "end": v(384.11, 250.55) * mm});
            skArc(sketch, "E297.0.7.10", {"start": v(416.75, 250.55) * mm, "mid": v(419.93, 247.37) * mm, "end": v(423.1, 250.55) * mm});
            skArc(sketch, "E297.0.7.11", {"start": v(384.11, 244.2) * mm, "mid": v(380.94, 241.02) * mm, "end": v(384.11, 237.85) * mm});
            skArc(sketch, "E297.0.7.12", {"start": v(357.06, 250.55) * mm, "mid": v(360.24, 247.37) * mm, "end": v(363.41, 250.55) * mm});
            skLineSegment(sketch, "E297.0.7.13", {"start": v(396.05, 237.85) * mm, "end": v(396.05, 250.55) * mm});
            skArc(sketch, "E297.0.7.14", {"start": v(363.41, 262.48) * mm, "mid": v(360.24, 265.66) * mm, "end": v(357.06, 262.48) * mm});
            skArc(sketch, "E297.0.7.15", {"start": v(396.05, 237.85) * mm, "mid": v(399.22, 241.02) * mm, "end": v(396.05, 244.2) * mm});
            skLineSegment(sketch, "E297.0.8.0", {"start": v(357.06, 364.08) * mm, "end": v(357.06, 352.15) * mm});
            skPoint(sketch, "E297.0.8.1", {"position": v(390.08, 352.15) * mm});
            skLineSegment(sketch, "E297.0.8.2", {"start": v(423.1, 364.08) * mm, "end": v(423.1, 352.15) * mm});
            skPoint(sketch, "E297.0.8.3", {"position": v(384.11, 364.85) * mm});
            skLineSegment(sketch, "E297.0.8.4", {"start": v(357.06, 364.08) * mm, "end": v(423.1, 364.08) * mm});
            skLineSegment(sketch, "E297.0.8.5", {"start": v(396.05, 339.45) * mm, "end": v(384.11, 339.45) * mm});
            skPoint(sketch, "E297.0.8.6", {"position": v(396.05, 364.85) * mm});
            skLineSegment(sketch, "E297.0.8.7", {"start": v(357.06, 352.15) * mm, "end": v(423.1, 352.15) * mm});
            skArc(sketch, "E297.0.8.8", {"start": v(423.1, 364.08) * mm, "mid": v(419.93, 367.26) * mm, "end": v(416.75, 364.08) * mm});
            skLineSegment(sketch, "E297.0.8.9", {"start": v(384.11, 339.45) * mm, "end": v(384.11, 352.15) * mm});
            skArc(sketch, "E297.0.8.10", {"start": v(416.75, 352.15) * mm, "mid": v(419.93, 348.97) * mm, "end": v(423.1, 352.15) * mm});
            skArc(sketch, "E297.0.8.11", {"start": v(384.11, 345.8) * mm, "mid": v(380.94, 342.62) * mm, "end": v(384.11, 339.45) * mm});
            skArc(sketch, "E297.0.8.12", {"start": v(357.06, 352.15) * mm, "mid": v(360.24, 348.97) * mm, "end": v(363.41, 352.15) * mm});
            skLineSegment(sketch, "E297.0.8.13", {"start": v(396.05, 339.45) * mm, "end": v(396.05, 352.15) * mm});
            skArc(sketch, "E297.0.8.14", {"start": v(363.41, 364.08) * mm, "mid": v(360.24, 367.26) * mm, "end": v(357.06, 364.08) * mm});
            skArc(sketch, "E297.0.8.15", {"start": v(396.05, 339.45) * mm, "mid": v(399.22, 342.62) * mm, "end": v(396.05, 345.8) * mm});
            skLineSegment(sketch, "E297.0.9.0", {"start": v(357.06, 465.68) * mm, "end": v(357.06, 453.75) * mm});
            skPoint(sketch, "E297.0.9.1", {"position": v(390.08, 453.75) * mm});
            skLineSegment(sketch, "E297.0.9.2", {"start": v(423.1, 465.68) * mm, "end": v(423.1, 453.75) * mm});
            skPoint(sketch, "E297.0.9.3", {"position": v(384.11, 466.45) * mm});
            skLineSegment(sketch, "E297.0.9.4", {"start": v(357.06, 465.68) * mm, "end": v(423.1, 465.68) * mm});
            skLineSegment(sketch, "E297.0.9.5", {"start": v(396.05, 441.05) * mm, "end": v(384.11, 441.05) * mm});
            skPoint(sketch, "E297.0.9.6", {"position": v(396.05, 466.45) * mm});
            skLineSegment(sketch, "E297.0.9.7", {"start": v(357.06, 453.75) * mm, "end": v(423.1, 453.75) * mm});
            skArc(sketch, "E297.0.9.8", {"start": v(423.1, 465.68) * mm, "mid": v(419.93, 468.86) * mm, "end": v(416.75, 465.68) * mm});
            skLineSegment(sketch, "E297.0.9.9", {"start": v(384.11, 441.05) * mm, "end": v(384.11, 453.75) * mm});
            skArc(sketch, "E297.0.9.10", {"start": v(416.75, 453.75) * mm, "mid": v(419.93, 450.57) * mm, "end": v(423.1, 453.75) * mm});
            skArc(sketch, "E297.0.9.11", {"start": v(384.11, 447.4) * mm, "mid": v(380.94, 444.22) * mm, "end": v(384.11, 441.05) * mm});
            skArc(sketch, "E297.0.9.12", {"start": v(357.06, 453.75) * mm, "mid": v(360.24, 450.57) * mm, "end": v(363.41, 453.75) * mm});
            skLineSegment(sketch, "E297.0.9.13", {"start": v(396.05, 441.05) * mm, "end": v(396.05, 453.75) * mm});
            skArc(sketch, "E297.0.9.14", {"start": v(363.41, 465.68) * mm, "mid": v(360.24, 468.86) * mm, "end": v(357.06, 465.68) * mm});
            skArc(sketch, "E297.0.9.15", {"start": v(396.05, 441.05) * mm, "mid": v(399.22, 444.22) * mm, "end": v(396.05, 447.4) * mm});
            skLineSegment(sketch, "E297.0.10.0", {"start": v(357.06, 567.28) * mm, "end": v(357.06, 555.35) * mm});
            skPoint(sketch, "E297.0.10.1", {"position": v(390.08, 555.35) * mm});
            skLineSegment(sketch, "E297.0.10.2", {"start": v(423.1, 567.28) * mm, "end": v(423.1, 555.35) * mm});
            skPoint(sketch, "E297.0.10.3", {"position": v(384.11, 568.05) * mm});
            skLineSegment(sketch, "E297.0.10.4", {"start": v(357.06, 567.28) * mm, "end": v(423.1, 567.28) * mm});
            skLineSegment(sketch, "E297.0.10.5", {"start": v(396.05, 542.65) * mm, "end": v(384.11, 542.65) * mm});
            skPoint(sketch, "E297.0.10.6", {"position": v(396.05, 568.05) * mm});
            skLineSegment(sketch, "E297.0.10.7", {"start": v(357.06, 555.35) * mm, "end": v(423.1, 555.35) * mm});
            skArc(sketch, "E297.0.10.8", {"start": v(423.1, 567.28) * mm, "mid": v(419.93, 570.46) * mm, "end": v(416.75, 567.28) * mm});
            skLineSegment(sketch, "E297.0.10.9", {"start": v(384.11, 542.65) * mm, "end": v(384.11, 555.35) * mm});
            skArc(sketch, "E297.0.10.10", {"start": v(416.75, 555.35) * mm, "mid": v(419.93, 552.17) * mm, "end": v(423.1, 555.35) * mm});
            skArc(sketch, "E297.0.10.11", {"start": v(384.11, 549) * mm, "mid": v(380.94, 545.82) * mm, "end": v(384.11, 542.65) * mm});
            skArc(sketch, "E297.0.10.12", {"start": v(357.06, 555.35) * mm, "mid": v(360.24, 552.17) * mm, "end": v(363.41, 555.35) * mm});
            skLineSegment(sketch, "E297.0.10.13", {"start": v(396.05, 542.65) * mm, "end": v(396.05, 555.35) * mm});
            skArc(sketch, "E297.0.10.14", {"start": v(363.41, 567.28) * mm, "mid": v(360.24, 570.46) * mm, "end": v(357.06, 567.28) * mm});
            skArc(sketch, "E297.0.10.15", {"start": v(396.05, 542.65) * mm, "mid": v(399.22, 545.82) * mm, "end": v(396.05, 549) * mm});
            skLineSegment(sketch, "E297.0.11.0", {"start": v(357.06, 668.88) * mm, "end": v(357.06, 656.95) * mm});
            skPoint(sketch, "E297.0.11.1", {"position": v(390.08, 656.95) * mm});
            skLineSegment(sketch, "E297.0.11.2", {"start": v(423.1, 668.88) * mm, "end": v(423.1, 656.95) * mm});
            skPoint(sketch, "E297.0.11.3", {"position": v(384.11, 669.65) * mm});
            skLineSegment(sketch, "E297.0.11.4", {"start": v(357.06, 668.88) * mm, "end": v(423.1, 668.88) * mm});
            skLineSegment(sketch, "E297.0.11.5", {"start": v(396.05, 644.25) * mm, "end": v(384.11, 644.25) * mm});
            skPoint(sketch, "E297.0.11.6", {"position": v(396.05, 669.65) * mm});
            skLineSegment(sketch, "E297.0.11.7", {"start": v(357.06, 656.95) * mm, "end": v(423.1, 656.95) * mm});
            skArc(sketch, "E297.0.11.8", {"start": v(423.1, 668.88) * mm, "mid": v(419.93, 672.06) * mm, "end": v(416.75, 668.88) * mm});
            skLineSegment(sketch, "E297.0.11.9", {"start": v(384.11, 644.25) * mm, "end": v(384.11, 656.95) * mm});
            skArc(sketch, "E297.0.11.10", {"start": v(416.75, 656.95) * mm, "mid": v(419.93, 653.77) * mm, "end": v(423.1, 656.95) * mm});
            skArc(sketch, "E297.0.11.11", {"start": v(384.11, 650.6) * mm, "mid": v(380.94, 647.42) * mm, "end": v(384.11, 644.25) * mm});
            skArc(sketch, "E297.0.11.12", {"start": v(357.06, 656.95) * mm, "mid": v(360.24, 653.77) * mm, "end": v(363.41, 656.95) * mm});
            skLineSegment(sketch, "E297.0.11.13", {"start": v(396.05, 644.25) * mm, "end": v(396.05, 656.95) * mm});
            skArc(sketch, "E297.0.11.14", {"start": v(363.41, 668.88) * mm, "mid": v(360.24, 672.06) * mm, "end": v(357.06, 668.88) * mm});
            skArc(sketch, "E297.0.11.15", {"start": v(396.05, 644.25) * mm, "mid": v(399.22, 647.42) * mm, "end": v(396.05, 650.6) * mm});
            skLineSegment(sketch, "E297.direction1", {"start": v(357.06, -460.65) * mm, "end": v(382.46, -460.65) * mm, "construction": true});
            skLineSegment(sketch, "E297.direction2", {"start": v(357.06, -460.65) * mm, "end": v(357.06, -359.05) * mm, "construction": true});
            skSolve(sketch);
        }
        {
            var Q0;
            Q0=qCreatedBy(makeId("Top.planeOp"),FACE);
            var sketch = newSketch(context, id + "F17", { "sketchPlane" : qUnion([Q0])});
            skLineSegment(sketch, "E298.bottom", {"start": v(1569.74, 81.98) * mm, "end": v(1684.04, 81.98) * mm});
            skLineSegment(sketch, "E298.top", {"start": v(1569.74, -32.32) * mm, "end": v(1684.04, -32.32) * mm});
            skLineSegment(sketch, "E298.left", {"start": v(1569.74, 81.98) * mm, "end": v(1569.74, -32.32) * mm});
            skLineSegment(sketch, "E298.right", {"start": v(1684.04, 81.98) * mm, "end": v(1684.04, -32.32) * mm});
            skPoint(sketch, "E299.visualSharp", {"position": v(2103.14, 0) * mm});
            skLineSegment(sketch, "E300.bottom", {"start": v(1946.13, 12.1) * mm, "end": v(1971.53, 12.1) * mm});
            skLineSegment(sketch, "E300.top", {"start": v(1946.13, -102.2) * mm, "end": v(1971.53, -102.2) * mm});
            skLineSegment(sketch, "E300.right", {"start": v(1971.53, 12.1) * mm, "end": v(1971.53, -13.3) * mm});
            skArc(sketch, "E301", {"start": v(1952.48, 12.1) * mm, "mid": v(1949.3, 15.27) * mm, "end": v(1946.13, 12.1) * mm});
            skLineSegment(sketch, "E302.filletArc", {"start": v(2039.17, 57.65) * mm, "end": v(2039.17, 57.65) * mm});
            skLineSegment(sketch, "E303.MirrorCS", {"start": v(2013.77, 57.65) * mm, "end": v(2013.77, 57.65) * mm});
            skArc(sketch, "E304.MirrorCS", {"start": v(1876.28, 12.1) * mm, "mid": v(1879.46, 15.27) * mm, "end": v(1882.63, 12.1) * mm});
            skLineSegment(sketch, "E305.MirrorCS", {"start": v(1882.63, 12.1) * mm, "end": v(1857.23, 12.1) * mm});
            skLineSegment(sketch, "E306.MirrorCS", {"start": v(1882.63, -102.2) * mm, "end": v(1876.28, -102.2) * mm});
            skLineSegment(sketch, "E307.MirrorCS", {"start": v(1857.23, 12.1) * mm, "end": v(1857.23, -13.3) * mm});
            skLineSegment(sketch, "E308.MirrorCS", {"start": v(1882.63, -102.2) * mm, "end": v(1863.58, -102.2) * mm});
            skArc(sketch, "E309", {"start": v(1971.53, 12.1) * mm, "mid": v(1968.36, 15.27) * mm, "end": v(1965.18, 12.1) * mm});
            skArc(sketch, "E310", {"start": v(1863.58, 12.1) * mm, "mid": v(1860.4, 15.27) * mm, "end": v(1857.23, 12.1) * mm});
            skLineSegment(sketch, "E311", {"start": v(1857.23, -45.05) * mm, "end": v(2035.55, -45.05) * mm, "construction": true});
            skPoint(sketch, "E311.endSnap0", {"position": v(1857.23, -45.05) * mm});
            skPoint(sketch, "E312", {"position": v(1914.38, -45.05) * mm});
            skLineSegment(sketch, "E313.top", {"start": v(1885.8, 5.75) * mm, "end": v(1942.96, 5.75) * mm});
            skLineSegment(sketch, "E313.left", {"start": v(1882.63, 12.1) * mm, "end": v(1882.63, 8.92) * mm});
            skLineSegment(sketch, "E313.right", {"start": v(1946.13, 12.1) * mm, "end": v(1946.13, 8.92) * mm});
            skLineSegment(sketch, "E314.bottom", {"start": v(1873.1, -13.3) * mm, "end": v(1857.23, -13.3) * mm});
            skLineSegment(sketch, "E314.top", {"start": v(1873.1, -76.8) * mm, "end": v(1857.23, -76.8) * mm});
            skLineSegment(sketch, "E314.left", {"start": v(1876.28, -16.48) * mm, "end": v(1876.28, -73.63) * mm});
            skLineSegment(sketch, "E315.bottom", {"start": v(1955.66, -13.3) * mm, "end": v(1971.53, -13.3) * mm});
            skLineSegment(sketch, "E315.top", {"start": v(1955.66, -76.8) * mm, "end": v(1971.53, -76.8) * mm});
            skLineSegment(sketch, "E315.left", {"start": v(1952.48, -16.48) * mm, "end": v(1952.48, -73.63) * mm});
            skPoint(sketch, "E315.middle", {"position": v(1971.53, -45.05) * mm});
            skArc(sketch, "E316.MirrorCS", {"start": v(1876.28, -102.2) * mm, "mid": v(1879.46, -105.38) * mm, "end": v(1882.63, -102.2) * mm});
            skArc(sketch, "E317.MirrorCS", {"start": v(1952.48, -102.2) * mm, "mid": v(1949.3, -105.38) * mm, "end": v(1946.13, -102.2) * mm});
            skArc(sketch, "E318.MirrorCS", {"start": v(1971.53, -102.2) * mm, "mid": v(1968.36, -105.38) * mm, "end": v(1965.18, -102.2) * mm});
            skArc(sketch, "E319.MirrorCS", {"start": v(1863.58, -102.2) * mm, "mid": v(1860.4, -105.38) * mm, "end": v(1857.23, -102.2) * mm});
            skLineSegment(sketch, "E320.MirrorCS", {"start": v(1882.63, -102.2) * mm, "end": v(1882.63, -99.03) * mm});
            skLineSegment(sketch, "E321.MirrorCS", {"start": v(1946.13, -102.2) * mm, "end": v(1946.13, -99.03) * mm});
            skLineSegment(sketch, "E322.MirrorCS", {"start": v(1885.8, -95.85) * mm, "end": v(1942.96, -95.85) * mm});
            skPoint(sketch, "E323.visualSharp", {"position": v(1876.28, -13.3) * mm});
            skArc(sketch, "E323.filletArc", {"start": v(1876.28, -16.48) * mm, "mid": v(1875.35, -14.23) * mm, "end": v(1873.1, -13.3) * mm});
            skPoint(sketch, "E324.visualSharp", {"position": v(1876.28, -76.8) * mm});
            skArc(sketch, "E324.filletArc", {"start": v(1873.1, -76.8) * mm, "mid": v(1875.35, -75.87) * mm, "end": v(1876.28, -73.63) * mm});
            skPoint(sketch, "E325.visualSharp", {"position": v(1882.63, -95.85) * mm});
            skArc(sketch, "E325.filletArc", {"start": v(1885.8, -95.85) * mm, "mid": v(1883.56, -96.78) * mm, "end": v(1882.63, -99.03) * mm});
            skPoint(sketch, "E326.visualSharp", {"position": v(1946.13, -95.85) * mm});
            skArc(sketch, "E326.filletArc", {"start": v(1946.13, -99.03) * mm, "mid": v(1945.2, -96.78) * mm, "end": v(1942.96, -95.85) * mm});
            skPoint(sketch, "E327.visualSharp", {"position": v(1952.48, -76.8) * mm});
            skArc(sketch, "E327.filletArc", {"start": v(1952.48, -73.63) * mm, "mid": v(1953.41, -75.87) * mm, "end": v(1955.66, -76.8) * mm});
            skPoint(sketch, "E328.visualSharp", {"position": v(1952.48, -13.3) * mm});
            skArc(sketch, "E328.filletArc", {"start": v(1955.66, -13.3) * mm, "mid": v(1953.41, -14.23) * mm, "end": v(1952.48, -16.48) * mm});
            skPoint(sketch, "E329.visualSharp", {"position": v(1946.13, 5.75) * mm});
            skArc(sketch, "E329.filletArc", {"start": v(1942.96, 5.75) * mm, "mid": v(1945.2, 6.68) * mm, "end": v(1946.13, 8.92) * mm});
            skPoint(sketch, "E330.visualSharp", {"position": v(1882.63, 5.75) * mm});
            skArc(sketch, "E330.filletArc", {"start": v(1882.63, 8.92) * mm, "mid": v(1883.56, 6.68) * mm, "end": v(1885.8, 5.75) * mm});
            skPoint(sketch, "E314.right.start.orphan", {"position": v(1838.18, -13.3) * mm});
            skPoint(sketch, "E331.orphan", {"position": v(1838.18, -76.8) * mm});
            skPoint(sketch, "E332.orphan", {"position": v(1990.58, -76.8) * mm});
            skPoint(sketch, "E315.right.start.orphan", {"position": v(1990.58, -13.3) * mm});
            skLineSegment(sketch, "E333.trimOffspring", {"start": v(1971.53, -76.8) * mm, "end": v(1971.53, -102.2) * mm});
            skLineSegment(sketch, "E334.trimOffspring", {"start": v(1857.23, -76.8) * mm, "end": v(1857.23, -102.2) * mm});
            skPoint(sketch, "E335.MirrorCS.start.orphan", {"position": v(1914.38, 12.1) * mm});
            skPoint(sketch, "E336.orphan", {"position": v(1857.23, -102.2) * mm});
            skPoint(sketch, "E337.MirrorCS.start.orphan", {"position": v(1914.38, -102.2) * mm});
            skPoint(sketch, "E338.orphan", {"position": v(1946.13, -102.2) * mm});
            skPoint(sketch, "E339.bottom.end.orphan", {"position": v(1946.13, 12.1) * mm});
            skLineSegment(sketch, "E340.bottom", {"start": v(1965.18, -121.25) * mm, "end": v(1863.58, -121.25) * mm});
            skLineSegment(sketch, "E340.top", {"start": v(1965.18, 31.15) * mm, "end": v(1863.58, 31.15) * mm});
            skLineSegment(sketch, "E340.left", {"start": v(1990.58, -95.85) * mm, "end": v(1990.58, 5.75) * mm});
            skLineSegment(sketch, "E340.right", {"start": v(1838.18, -95.85) * mm, "end": v(1838.18, 5.75) * mm});
            skLineSegment(sketch, "E341.bottom", {"start": v(2286.4, 19.76) * mm, "end": v(2311.8, 19.76) * mm});
            skLineSegment(sketch, "E341.top", {"start": v(2286.4, -94.54) * mm, "end": v(2311.8, -94.54) * mm});
            skLineSegment(sketch, "E341.right", {"start": v(2311.8, 19.76) * mm, "end": v(2311.8, -5.64) * mm});
            skArc(sketch, "E342", {"start": v(2292.74, 19.76) * mm, "mid": v(2289.57, 22.94) * mm, "end": v(2286.4, 19.76) * mm});
            skArc(sketch, "E343.MirrorCS", {"start": v(2216.54, 19.76) * mm, "mid": v(2219.72, 22.94) * mm, "end": v(2222.9, 19.76) * mm});
            skLineSegment(sketch, "E344.MirrorCS", {"start": v(2222.9, 19.76) * mm, "end": v(2197.5, 19.76) * mm});
            skLineSegment(sketch, "E345.MirrorCS", {"start": v(2222.9, -94.54) * mm, "end": v(2216.54, -94.54) * mm});
            skLineSegment(sketch, "E346.MirrorCS", {"start": v(2197.5, 19.76) * mm, "end": v(2197.5, -5.64) * mm});
            skLineSegment(sketch, "E347.MirrorCS", {"start": v(2222.9, -94.54) * mm, "end": v(2203.84, -94.54) * mm});
            skArc(sketch, "E348", {"start": v(2311.8, 19.76) * mm, "mid": v(2308.62, 22.94) * mm, "end": v(2305.44, 19.76) * mm});
            skArc(sketch, "E349", {"start": v(2203.84, 19.76) * mm, "mid": v(2200.67, 22.94) * mm, "end": v(2197.5, 19.76) * mm});
            skPoint(sketch, "E350.endSnap0", {"position": v(2197.5, -37.39) * mm});
            skPoint(sketch, "E351", {"position": v(2254.64, -37.39) * mm});
            skLineSegment(sketch, "E352.top", {"start": v(2226.07, 13.41) * mm, "end": v(2283.22, 13.41) * mm});
            skLineSegment(sketch, "E352.left", {"start": v(2222.9, 19.76) * mm, "end": v(2222.9, 16.59) * mm});
            skLineSegment(sketch, "E352.right", {"start": v(2286.4, 19.76) * mm, "end": v(2286.4, 16.59) * mm});
            skLineSegment(sketch, "E353.bottom", {"start": v(2213.37, -5.64) * mm, "end": v(2197.5, -5.64) * mm});
            skLineSegment(sketch, "E353.top", {"start": v(2213.37, -69.14) * mm, "end": v(2197.5, -69.14) * mm});
            skLineSegment(sketch, "E353.left", {"start": v(2216.54, -8.81) * mm, "end": v(2216.54, -65.96) * mm});
            skLineSegment(sketch, "E354.bottom", {"start": v(2295.92, -5.64) * mm, "end": v(2311.8, -5.64) * mm});
            skLineSegment(sketch, "E354.top", {"start": v(2295.92, -69.14) * mm, "end": v(2311.8, -69.14) * mm});
            skLineSegment(sketch, "E354.left", {"start": v(2292.74, -8.81) * mm, "end": v(2292.74, -65.96) * mm});
            skPoint(sketch, "E354.middle", {"position": v(2311.8, -37.39) * mm});
            skArc(sketch, "E355.MirrorCS", {"start": v(2216.54, -94.54) * mm, "mid": v(2219.72, -97.71) * mm, "end": v(2222.9, -94.54) * mm});
            skArc(sketch, "E356.MirrorCS", {"start": v(2292.74, -94.54) * mm, "mid": v(2289.57, -97.71) * mm, "end": v(2286.4, -94.54) * mm});
            skArc(sketch, "E357.MirrorCS", {"start": v(2311.8, -94.54) * mm, "mid": v(2308.62, -97.71) * mm, "end": v(2305.44, -94.54) * mm});
            skArc(sketch, "E358.MirrorCS", {"start": v(2203.84, -94.54) * mm, "mid": v(2200.67, -97.71) * mm, "end": v(2197.5, -94.54) * mm});
            skLineSegment(sketch, "E359.MirrorCS", {"start": v(2222.9, -94.54) * mm, "end": v(2222.9, -91.36) * mm});
            skLineSegment(sketch, "E360.MirrorCS", {"start": v(2286.4, -94.54) * mm, "end": v(2286.4, -91.36) * mm});
            skLineSegment(sketch, "E361.MirrorCS", {"start": v(2226.07, -88.19) * mm, "end": v(2283.22, -88.19) * mm});
            skPoint(sketch, "E362.visualSharp", {"position": v(2216.54, -5.64) * mm});
            skArc(sketch, "E362.filletArc", {"start": v(2216.54, -8.81) * mm, "mid": v(2215.61, -6.57) * mm, "end": v(2213.37, -5.64) * mm});
            skPoint(sketch, "E363.visualSharp", {"position": v(2216.54, -69.14) * mm});
            skArc(sketch, "E363.filletArc", {"start": v(2213.37, -69.14) * mm, "mid": v(2215.61, -68.2) * mm, "end": v(2216.54, -65.96) * mm});
            skPoint(sketch, "E364.visualSharp", {"position": v(2222.9, -88.19) * mm});
            skArc(sketch, "E364.filletArc", {"start": v(2226.07, -88.19) * mm, "mid": v(2223.82, -89.12) * mm, "end": v(2222.9, -91.36) * mm});
            skPoint(sketch, "E365.visualSharp", {"position": v(2286.4, -88.19) * mm});
            skArc(sketch, "E365.filletArc", {"start": v(2286.4, -91.36) * mm, "mid": v(2285.46, -89.12) * mm, "end": v(2283.22, -88.19) * mm});
            skPoint(sketch, "E366.visualSharp", {"position": v(2292.74, -69.14) * mm});
            skArc(sketch, "E366.filletArc", {"start": v(2292.74, -65.96) * mm, "mid": v(2293.67, -68.2) * mm, "end": v(2295.92, -69.14) * mm});
            skPoint(sketch, "E367.visualSharp", {"position": v(2292.74, -5.64) * mm});
            skArc(sketch, "E367.filletArc", {"start": v(2295.92, -5.64) * mm, "mid": v(2293.67, -6.57) * mm, "end": v(2292.74, -8.81) * mm});
            skPoint(sketch, "E368.visualSharp", {"position": v(2286.4, 13.41) * mm});
            skArc(sketch, "E368.filletArc", {"start": v(2283.22, 13.41) * mm, "mid": v(2285.46, 14.34) * mm, "end": v(2286.4, 16.59) * mm});
            skPoint(sketch, "E369.visualSharp", {"position": v(2222.9, 13.41) * mm});
            skArc(sketch, "E369.filletArc", {"start": v(2222.9, 16.59) * mm, "mid": v(2223.82, 14.34) * mm, "end": v(2226.07, 13.41) * mm});
            skPoint(sketch, "E353.right.start.orphan", {"position": v(2178.44, -5.64) * mm});
            skPoint(sketch, "E370.orphan", {"position": v(2178.44, -69.14) * mm});
            skPoint(sketch, "E371.orphan", {"position": v(2330.84, -69.14) * mm});
            skPoint(sketch, "E354.right.start.orphan", {"position": v(2330.84, -5.64) * mm});
            skLineSegment(sketch, "E372.trimOffspring", {"start": v(2311.8, -69.14) * mm, "end": v(2311.8, -94.54) * mm});
            skLineSegment(sketch, "E373.trimOffspring", {"start": v(2197.5, -69.14) * mm, "end": v(2197.5, -94.54) * mm});
            skPoint(sketch, "E374.MirrorCS.start.orphan", {"position": v(2254.64, 19.76) * mm});
            skPoint(sketch, "E375.orphan", {"position": v(2197.5, -94.54) * mm});
            skPoint(sketch, "E376.MirrorCS.start.orphan", {"position": v(2254.64, -94.54) * mm});
            skPoint(sketch, "E377.orphan", {"position": v(2286.4, -94.54) * mm});
            skPoint(sketch, "E378.bottom.end.orphan", {"position": v(2286.4, 19.76) * mm});
            skLineSegment(sketch, "E379.bottom", {"start": v(2330.84, -113.59) * mm, "end": v(2178.44, -113.59) * mm});
            skLineSegment(sketch, "E379.top", {"start": v(2330.84, 38.81) * mm, "end": v(2178.44, 38.81) * mm});
            skLineSegment(sketch, "E379.left", {"start": v(2330.84, -113.59) * mm, "end": v(2330.84, 38.81) * mm});
            skLineSegment(sketch, "E379.right", {"start": v(2178.44, -113.59) * mm, "end": v(2178.44, 38.81) * mm});
            skPoint(sketch, "E380.visualSharp", {"position": v(1838.18, 31.15) * mm});
            skArc(sketch, "E380.filletArc", {"start": v(1863.58, 31.15) * mm, "mid": v(1845.62, 23.7) * mm, "end": v(1838.18, 5.75) * mm});
            skPoint(sketch, "E381.visualSharp", {"position": v(1990.58, 31.15) * mm});
            skArc(sketch, "E381.filletArc", {"start": v(1990.58, 5.75) * mm, "mid": v(1983.14, 23.7) * mm, "end": v(1965.18, 31.15) * mm});
            skPoint(sketch, "E382.visualSharp", {"position": v(1990.58, -121.25) * mm});
            skArc(sketch, "E382.filletArc", {"start": v(1965.18, -121.25) * mm, "mid": v(1983.14, -113.81) * mm, "end": v(1990.58, -95.85) * mm});
            skPoint(sketch, "E383.visualSharp", {"position": v(1838.18, -121.25) * mm});
            skArc(sketch, "E383.filletArc", {"start": v(1838.18, -95.85) * mm, "mid": v(1845.62, -113.81) * mm, "end": v(1863.58, -121.25) * mm});
            skArc(sketch, "E384", {"start": v(1857.23, -76.8) * mm, "mid": v(1854.06, -79.98) * mm, "end": v(1857.23, -83.15) * mm});
            skArc(sketch, "E385", {"start": v(1857.23, -6.95) * mm, "mid": v(1854.06, -10.13) * mm, "end": v(1857.23, -13.3) * mm});
            skLineSegment(sketch, "E386", {"start": v(1914.38, -45.05) * mm, "end": v(1914.38, -81.23) * mm, "construction": true});
            skArc(sketch, "E387.MirrorCS", {"start": v(1971.53, -76.8) * mm, "mid": v(1974.7, -79.98) * mm, "end": v(1971.53, -83.15) * mm});
            skArc(sketch, "E388.MirrorCS", {"start": v(1971.53, -6.95) * mm, "mid": v(1974.7, -10.13) * mm, "end": v(1971.53, -13.3) * mm});
            skLineSegment(sketch, "E389.bottom", {"start": v(1909.05, -233.44) * mm, "end": v(1818.12, -233.44) * mm});
            skLineSegment(sketch, "E389.top", {"start": v(1909.05, -142.5) * mm, "end": v(1818.12, -142.5) * mm});
            skLineSegment(sketch, "E389.left", {"start": v(1909.05, -233.44) * mm, "end": v(1909.05, -142.5) * mm});
            skLineSegment(sketch, "E389.right", {"start": v(1818.12, -233.44) * mm, "end": v(1818.12, -142.5) * mm});
            skPoint(sketch, "E389.middle", {"position": v(1863.58, -187.97) * mm});
            skSolve(sketch);
        }
        {
            var Q0;
            Q0 = qSketchRegion(id + "F16", true);
            extrude(context, id + "F18", {"entities" : qUnion([Q0]), "depth" : 11.58 * mm});
        }
        {
            var Q0;
            Q0=makeQuery(id+"F17.imprint","IMPRINT",FACE,{"disambiguationData":[TD([[makeQuery(id+"F17.imprint","IMPRINT",EDGE,{"derivedFrom":sQuery(id+"F17.wireOp",EDGE,"E298.bottom")}),-1.0]])]});
            var Q1;
            {var subQ2=sQuery(id+"F17.wireOp",EDGE,"E301");Q1=makeQuery(id+"F17.imprint","IMPRINT",FACE,{"disambiguationData":[TD([[makeQuery(id+"F17.imprint","IMPRINT",EDGE,{"derivedFrom":subQ2}),-1.0]])]});}
            extrude(context, id + "F19", {"entities" : qUnion([Q0, Q1]), "depth" : 11.68 * mm});
        }
        {
            var Q0;
            Q0=makeQuery(id+"F17.imprint","IMPRINT",FACE,{"disambiguationData":[TD([[makeQuery(id+"F17.imprint","IMPRINT",EDGE,{"derivedFrom":sQuery(id+"F17.wireOp",EDGE,"E389.bottom")}),-1.0]])]});
            extrude(context, id + "F20", {"entities" : qUnion([Q0]), "depth" : 11.68 * mm});
        }
        {
            var Q0;
            Q0=qCreatedBy(makeId("Top.planeOp"),FACE);
            var sketch = newSketch(context, id + "F21", { "sketchPlane" : qUnion([Q0])});
            skPoint(sketch, "E390.visualSharp", {"position": v(1493.79, -269.17) * mm});
            skArc(sketch, "E390.filletArc", {"start": v(1493.79, -370.77) * mm, "mid": v(1464.03, -298.93) * mm, "end": v(1392.19, -269.17) * mm});
            skPoint(sketch, "E391.visualSharp", {"position": v(1493.79, -612.07) * mm});
            skLineSegment(sketch, "E392.top", {"start": v(1296.94, -497.77) * mm, "end": v(1328.69, -497.77) * mm});
            skLineSegment(sketch, "E393.bottom", {"start": v(1328.69, -497.77) * mm, "end": v(1354.09, -497.77) * mm});
            skLineSegment(sketch, "E393.left", {"start": v(1328.69, -497.77) * mm, "end": v(1328.69, -608.9) * mm});
            skLineSegment(sketch, "E393.right", {"start": v(1354.09, -497.77) * mm, "end": v(1354.09, -612.07) * mm});
            skArc(sketch, "E394", {"start": v(1335.04, -497.77) * mm, "mid": v(1331.86, -494.6) * mm, "end": v(1328.69, -497.77) * mm});
            skLineSegment(sketch, "E395.filletArc", {"start": v(16.78, -65.97) * mm, "end": v(16.78, -65.97) * mm});
            skLineSegment(sketch, "E396.MirrorCS", {"start": v(-8.62, -65.97) * mm, "end": v(-8.62, -65.97) * mm});
            skArc(sketch, "E397.MirrorCS", {"start": v(1258.84, -497.77) * mm, "mid": v(1262.01, -494.6) * mm, "end": v(1265.19, -497.77) * mm});
            skLineSegment(sketch, "E398.MirrorCS", {"start": v(1265.19, -497.77) * mm, "end": v(1239.79, -497.77) * mm});
            skLineSegment(sketch, "E399.MirrorCS", {"start": v(1296.94, -497.77) * mm, "end": v(1265.19, -497.77) * mm});
            skLineSegment(sketch, "E400.MirrorCS", {"start": v(1239.79, -497.77) * mm, "end": v(1239.79, -612.07) * mm});
            skLineSegment(sketch, "E401.MirrorCS", {"start": v(1265.19, -608.9) * mm, "end": v(1265.19, -497.77) * mm});
            skLineSegment(sketch, "E402.MirrorCS", {"start": v(1296.94, -612.07) * mm, "end": v(1325.51, -612.07) * mm});
            skLineSegment(sketch, "E403.MirrorCS", {"start": v(1296.94, -612.07) * mm, "end": v(1268.36, -612.07) * mm});
            skFitSpline(sketch, "E404", {"points": [v(1354.09, -612.07) * mm, v(1360.96, -612.07) * mm, v(1370.7, -602.24) * mm, v(1379.15, -578.52) * mm, v(1393.77, -550.91) * mm, v(1422.04, -521.67) * mm, v(1467.52, -500.88) * mm, v(1480.84, -496.98) * mm, v(1491.88, -488.54) * mm, v(1495.85, -450.4) * mm, v(1493.79, -370.77) * mm], "startDerivative": vector(133.06, -25.03) * mm, "endDerivative": vector(-44.6, 1613.14) * mm});
            skFitSpline(sketch, "E405.MirrorCS", {"points": [v(1239.79, -612.07) * mm, v(1232.91, -612.07) * mm, v(1223.17, -602.24) * mm, v(1214.72, -578.52) * mm, v(1200.1, -550.91) * mm, v(1171.84, -521.67) * mm, v(1126.35, -500.88) * mm, v(1113.03, -496.98) * mm, v(1101.99, -488.54) * mm, v(1098.02, -450.4) * mm, v(1100.09, -370.77) * mm], "startDerivative": vector(-133.06, -25.03) * mm, "endDerivative": vector(44.6, 1613.14) * mm});
            skLineSegment(sketch, "E406.MirrorCS", {"start": v(1392.19, -269.17) * mm, "end": v(1201.69, -269.17) * mm});
            skPoint(sketch, "E407.MirrorP", {"position": v(1100.09, -269.17) * mm});
            skArc(sketch, "E408.MirrorCS", {"start": v(1100.09, -370.77) * mm, "mid": v(1129.84, -298.93) * mm, "end": v(1201.69, -269.17) * mm});
            skPoint(sketch, "E409.MirrorP", {"position": v(1100.09, -612.07) * mm});
            skArc(sketch, "E410", {"start": v(1354.09, -497.77) * mm, "mid": v(1350.91, -494.6) * mm, "end": v(1347.74, -497.77) * mm});
            skArc(sketch, "E411", {"start": v(1246.14, -497.77) * mm, "mid": v(1242.96, -494.6) * mm, "end": v(1239.79, -497.77) * mm});
            skPoint(sketch, "E412.visualSharp", {"position": v(1265.19, -612.07) * mm});
            skArc(sketch, "E412.filletArc", {"start": v(1265.19, -608.9) * mm, "mid": v(1266.12, -611.14) * mm, "end": v(1268.36, -612.07) * mm});
            skArc(sketch, "E413.filletArc", {"start": v(1325.51, -612.07) * mm, "mid": v(1327.76, -611.14) * mm, "end": v(1328.69, -608.9) * mm});
            skPoint(sketch, "E414.visualSharp", {"position": v(1944.97, -377.17) * mm});
            skArc(sketch, "E414.filletArc", {"start": v(1944.97, -478.77) * mm, "mid": v(1915.21, -406.93) * mm, "end": v(1843.37, -377.17) * mm});
            skPoint(sketch, "E415.visualSharp", {"position": v(1944.97, -720.07) * mm});
            skLineSegment(sketch, "E416.top", {"start": v(1748.12, -605.77) * mm, "end": v(1779.87, -605.77) * mm});
            skLineSegment(sketch, "E417.bottom", {"start": v(1779.87, -605.77) * mm, "end": v(1805.27, -605.77) * mm});
            skLineSegment(sketch, "E417.left", {"start": v(1779.87, -605.77) * mm, "end": v(1779.87, -716.9) * mm});
            skLineSegment(sketch, "E417.right", {"start": v(1805.27, -605.77) * mm, "end": v(1805.27, -720.07) * mm});
            skArc(sketch, "E418", {"start": v(1786.22, -605.77) * mm, "mid": v(1783.05, -602.6) * mm, "end": v(1779.87, -605.77) * mm});
            skArc(sketch, "E419.MirrorCS", {"start": v(1710.02, -605.77) * mm, "mid": v(1713.2, -602.6) * mm, "end": v(1716.37, -605.77) * mm});
            skLineSegment(sketch, "E420.MirrorCS", {"start": v(1716.37, -605.77) * mm, "end": v(1690.97, -605.77) * mm});
            skLineSegment(sketch, "E421.MirrorCS", {"start": v(1748.12, -605.77) * mm, "end": v(1716.37, -605.77) * mm});
            skLineSegment(sketch, "E422.MirrorCS", {"start": v(1690.97, -605.77) * mm, "end": v(1690.97, -720.07) * mm});
            skLineSegment(sketch, "E423.MirrorCS", {"start": v(1716.37, -716.9) * mm, "end": v(1716.37, -605.77) * mm});
            skLineSegment(sketch, "E424.MirrorCS", {"start": v(1748.12, -720.07) * mm, "end": v(1776.7, -720.07) * mm});
            skLineSegment(sketch, "E425.MirrorCS", {"start": v(1748.12, -720.07) * mm, "end": v(1719.55, -720.07) * mm});
            skFitSpline(sketch, "E426", {"points": [v(1805.27, -720.07) * mm, v(1812.15, -720.07) * mm, v(1821.9, -710.24) * mm, v(1830.34, -686.52) * mm, v(1844.96, -658.9) * mm, v(1873.22, -629.67) * mm, v(1918.7, -608.88) * mm, v(1932.02, -604.98) * mm, v(1943.07, -596.53) * mm, v(1947.04, -558.4) * mm, v(1944.97, -478.77) * mm], "startDerivative": vector(133.06, -25.03) * mm, "endDerivative": vector(-44.6, 1613.14) * mm});
            skFitSpline(sketch, "E427.MirrorCS", {"points": [v(1690.97, -720.07) * mm, v(1684.1, -720.07) * mm, v(1674.35, -710.24) * mm, v(1665.9, -686.52) * mm, v(1651.28, -658.9) * mm, v(1623.02, -629.67) * mm, v(1577.54, -608.88) * mm, v(1564.22, -604.98) * mm, v(1553.17, -596.53) * mm, v(1549.2, -558.4) * mm, v(1551.27, -478.77) * mm], "startDerivative": vector(-133.06, -25.03) * mm, "endDerivative": vector(44.6, 1613.14) * mm});
            skLineSegment(sketch, "E428.MirrorCS", {"start": v(1843.37, -377.17) * mm, "end": v(1652.87, -377.17) * mm});
            skPoint(sketch, "E429.MirrorP", {"position": v(1551.27, -377.17) * mm});
            skArc(sketch, "E430.MirrorCS", {"start": v(1551.27, -478.77) * mm, "mid": v(1581.03, -406.93) * mm, "end": v(1652.87, -377.17) * mm});
            skPoint(sketch, "E431.MirrorP", {"position": v(1551.27, -720.07) * mm});
            skArc(sketch, "E432", {"start": v(1805.27, -605.77) * mm, "mid": v(1802.1, -602.6) * mm, "end": v(1798.92, -605.77) * mm});
            skArc(sketch, "E433", {"start": v(1697.32, -605.77) * mm, "mid": v(1694.15, -602.6) * mm, "end": v(1690.97, -605.77) * mm});
            skPoint(sketch, "E434.visualSharp", {"position": v(1716.37, -720.07) * mm});
            skArc(sketch, "E434.filletArc", {"start": v(1716.37, -716.9) * mm, "mid": v(1717.3, -719.14) * mm, "end": v(1719.55, -720.07) * mm});
            skArc(sketch, "E435.filletArc", {"start": v(1776.7, -720.07) * mm, "mid": v(1778.94, -719.14) * mm, "end": v(1779.87, -716.9) * mm});
            skCircle(sketch, "E436", {"center": v(1748.12, -529.13) * mm, "radius": 60.96 * mm});
            skCircle(sketch, "E437", {"center": v(1748.12, -529.13) * mm, "radius": 76.2 * mm});
            skLineSegment(sketch, "E438", {"start": v(1748.12, -529.13) * mm, "end": v(1748.12, -661.6) * mm, "construction": true});
            skFitSpline(sketch, "E439", {"points": [v(1824.32, -529.13) * mm, v(1823.79, -561.11) * mm, v(1814.04, -600.92) * mm, v(1810.42, -633.21) * mm, v(1805.27, -639.9) * mm], "startDerivative": vector(8.22, -234.18) * mm, "endDerivative": vector(-42.2, -35.4) * mm});
            skFitSpline(sketch, "E440.MirrorCS", {"points": [v(1671.92, -529.13) * mm, v(1672.46, -561.11) * mm, v(1682.2, -600.92) * mm, v(1685.82, -633.21) * mm, v(1690.97, -639.9) * mm], "startDerivative": vector(-8.22, -234.18) * mm, "endDerivative": vector(42.2, -35.4) * mm});
            skCircle(sketch, "E441", {"center": v(1375.52, -387.32) * mm, "radius": 60.96 * mm});
            skCircle(sketch, "E442", {"center": v(1375.52, -387.32) * mm, "radius": 76.2 * mm});
            skLineSegment(sketch, "E443", {"start": v(1296.94, -497.77) * mm, "end": v(1296.94, -294.55) * mm, "construction": true});
            skCircle(sketch, "E444.MirrorC", {"center": v(1218.35, -387.32) * mm, "radius": 76.2 * mm});
            skCircle(sketch, "E445.MirrorC", {"center": v(1218.35, -387.32) * mm, "radius": 60.96 * mm});
            skArc(sketch, "E446", {"start": v(1267.19, -328.83) * mm, "mid": v(1296.94, -339.94) * mm, "end": v(1326.69, -328.83) * mm});
            skLineSegment(sketch, "E447", {"start": v(1262.5, -387.32) * mm, "end": v(1338.97, -387.32) * mm, "construction": true});
            skFitSpline(sketch, "E448", {"points": [v(1161.15, -437.66) * mm, v(1212.5, -493.88) * mm, v(1234.35, -542.88) * mm, v(1239.79, -547.18) * mm], "startDerivative": vector(124.05, -108.8) * mm, "endDerivative": vector(37.85, -16.77) * mm});
            skFitSpline(sketch, "E449.MirrorCS", {"points": [v(1432.73, -437.66) * mm, v(1381.37, -493.88) * mm, v(1359.52, -542.88) * mm, v(1354.09, -547.18) * mm], "startDerivative": vector(-124.05, -108.8) * mm, "endDerivative": vector(-37.85, -16.77) * mm});
            skSolve(sketch);
        }
        {
            var Q0;
            Q0=makeQuery(id+"F21.imprint","IMPRINT",FACE,{"disambiguationData":[TD([[makeQuery(id+"F21.imprint","IMPRINT",EDGE,{"derivedFrom":sQuery(id+"F21.wireOp",EDGE,"E416.top")}),1.0]])]});
            var Q1;
            Q1=makeQuery(id+"F21.imprint","IMPRINT",FACE,{"disambiguationData":[TD([[makeQuery(id+"F21.imprint","IMPRINT",EDGE,{"derivedFrom":sQuery(id+"F21.wireOp",EDGE,"E436")}),-1.0]])]});
            var Q2;
            Q2=makeQuery(id+"F21.imprint","IMPRINT",FACE,{"disambiguationData":[TD([[makeQuery(id+"F21.imprint","IMPRINT",EDGE,{"derivedFrom":sQuery(id+"F21.wireOp",EDGE,"E416.top")}),-1.0]])]});
            extrude(context, id + "F22", {"entities" : qUnion([Q0, Q1, Q2]), "depth" : 11.94 * mm});
        }
        {
            var Q0;
            Q0=makeQuery(id+"F21.imprint","IMPRINT",FACE,{"disambiguationData":[TD([[makeQuery(id+"F21.imprint","IMPRINT",EDGE,{"derivedFrom":sQuery(id+"F21.wireOp",EDGE,"E445.MirrorC")}),1.0]])]});
            var Q1;
            Q1=makeQuery(id+"F21.imprint","IMPRINT",FACE,{"disambiguationData":[TD([[makeQuery(id+"F21.imprint","IMPRINT",EDGE,{"derivedFrom":sQuery(id+"F21.wireOp",EDGE,"E441")}),-1.0]])]});
            var Q2;
            Q2=makeQuery(id+"F21.imprint","IMPRINT",FACE,{"disambiguationData":[TD([[makeQuery(id+"F21.imprint","IMPRINT",EDGE,{"derivedFrom":sQuery(id+"F21.wireOp",EDGE,"E392.top")}),1.0]])]});
            var Q3;
            {var subQ0=sQuery(id+"F21.wireOp",EDGE,"E448");var subQ1=sQuery(id+"F21.wireOp",EDGE,"E444.MirrorC");var subQ2=makeQuery(id+"F21.imprint","INTERSECT",VERTEX,{"disambiguationData":[OD(0.0)],"derivedFrom":[subQ1,subQ0]});Q3=makeQuery(id+"F21.imprint","IMPRINT",FACE,{"disambiguationData":[TD([[makeQuery(id+"F21.imprint","IMPRINT",EDGE,{"disambiguationData":[TD([[subQ2,1.0]])],"derivedFrom":subQ1}),-1.0]])]});}
            var Q4;
            {var subQ0=sQuery(id+"F21.wireOp",EDGE,"E449.MirrorCS");var subQ1=sQuery(id+"F21.wireOp",EDGE,"E442");var subQ2=makeQuery(id+"F21.imprint","INTERSECT",VERTEX,{"disambiguationData":[OD(0.0)],"derivedFrom":[subQ1,subQ0]});Q4=makeQuery(id+"F21.imprint","IMPRINT",FACE,{"disambiguationData":[TD([[makeQuery(id+"F21.imprint","IMPRINT",EDGE,{"disambiguationData":[TD([[subQ2,1.0]])],"derivedFrom":subQ1}),1.0]])]});}
            var Q5;
            Q5=makeQuery(id+"F21.imprint","IMPRINT",FACE,{"disambiguationData":[TD([[makeQuery(id+"F21.imprint","IMPRINT",EDGE,{"derivedFrom":sQuery(id+"F21.wireOp",EDGE,"E392.top")}),-1.0]])]});
            extrude(context, id + "F23", {"entities" : qUnion([Q0, Q1, Q2, Q3, Q4, Q5]), "depth" : 11.94 * mm});
        }
    });
